# Revit family: ALW-L_приток
name_source: partatom
category: Воздухораспределители
revit_build: Autodesk Revit 2014 (Build: 20130308_1515(x64)
units: mm (PartAtom-declared; Revit-internal decimal feet)

## types (1242) — shared parameters
A = 23 мм
URL = http://inplast.ru
margins = 10 мм
Изготовитель = INPLAST-SMAY
Описание = Однорядная решетка с горизонтальными направляющими

## per-type parameters (varying)
| type | Aef | C' | D | n | С | Тип крепежа |
| ALW-L-100х100-АL | 0.006 м² | 95 мм | 100 мм | 10 | 100 мм | саморезы |
| ALW-L-125х100-АL | 0.008 м² | 120 мм | 100 мм | 10 | 125 мм | саморезы |
| ALW-L-125х125-АL | 0.009 м² | 120 мм | 125 мм | 13 | 125 мм | саморезы |
| ALW-L-150х100-АL | 0.009 м² | 145 мм | 100 мм | 10 | 150 мм | саморезы |
| ALW-L-150х125-АL | 0.011 м² | 145 мм | 125 мм | 13 | 150 мм | саморезы |
| ALW-L-150х150-АL | 0.014 м² | 145 мм | 150 мм | 15 | 150 мм | саморезы |
| ALW-L-200х100-АL | 0.012 м² | 195 мм | 100 мм | 10 | 200 мм | саморезы |
| ALW-L-200х125-АL | 0.015 м² | 195 мм | 125 мм | 13 | 200 мм | саморезы |
| ALW-L-200х150-АL | 0.018 м² | 195 мм | 150 мм | 15 | 200 мм | саморезы |
| ALW-L-200х200-АL | 0.024 м² | 195 мм | 200 мм | 20 | 200 мм | саморезы |
| ALW-L-225х100-АL | 0.014 м² | 220 мм | 100 мм | 10 | 225 мм | саморезы |
| ALW-L-225х125-АL | 0.017 м² | 220 мм | 125 мм | 13 | 225 мм | саморезы |
| ALW-L-225х150-АL | 0.020 м² | 220 мм | 150 мм | 15 | 225 мм | саморезы |
| ALW-L-225х200-АL | 0.027 м² | 220 мм | 200 мм | 20 | 225 мм | саморезы |
| ALW-L-225х225-АL | 0.030 м² | 220 мм | 225 мм | 23 | 225 мм | саморезы |
| ALW-L-250х100-АL | 0.015 м² | 245 мм | 100 мм | 10 | 250 мм | саморезы |
| ALW-L-250х125-АL | 0.019 м² | 245 мм | 125 мм | 13 | 250 мм | саморезы |
| ALW-L-250х150-АL | 0.023 м² | 245 мм | 150 мм | 15 | 250 мм | саморезы |
| ALW-L-250х200-АL | 0.030 м² | 245 мм | 200 мм | 20 | 250 мм | саморезы |
| ALW-L-250х225-АL | 0.034 м² | 245 мм | 225 мм | 23 | 250 мм | саморезы |
| ALW-L-250х250-АL | 0.038 м² | 245 мм | 250 мм | 25 | 250 мм | саморезы |
| ALW-L-300х100-АL | 0.018 м² | 295 мм | 100 мм | 10 | 300 мм | саморезы |
| ALW-L-300х125-АL | 0.023 м² | 295 мм | 125 мм | 13 | 300 мм | саморезы |
| ALW-L-300х150-АL | 0.027 м² | 295 мм | 150 мм | 15 | 300 мм | саморезы |
| ALW-L-300х200-АL | 0.036 м² | 295 мм | 200 мм | 20 | 300 мм | саморезы |
| ALW-L-300х225-АL | 0.041 м² | 295 мм | 225 мм | 23 | 300 мм | саморезы |
| ALW-L-300х250-АL | 0.045 м² | 295 мм | 250 мм | 25 | 300 мм | саморезы |
| ALW-L-300х300-АL | 0.054 м² | 295 мм | 300 мм | 30 | 300 мм | саморезы |
| ALW-L-325х100-АL | 0.020 м² | 320 мм | 100 мм | 10 | 325 мм | саморезы |
| ALW-L-325х125-АL | 0.024 м² | 320 мм | 125 мм | 13 | 325 мм | саморезы |
| ALW-L-325х150-АL | 0.029 м² | 320 мм | 150 мм | 15 | 325 мм | саморезы |
| ALW-L-325х200-АL | 0.039 м² | 320 мм | 200 мм | 20 | 325 мм | саморезы |
| ALW-L-325х225-АL | 0.044 м² | 320 мм | 225 мм | 23 | 325 мм | саморезы |
| ALW-L-325х250-АL | 0.049 м² | 320 мм | 250 мм | 25 | 325 мм | саморезы |
| ALW-L-325х300-АL | 0.059 м² | 320 мм | 300 мм | 30 | 325 мм | саморезы |
| ALW-L-325х325-АL | 0.064 м² | 320 мм | 325 мм | 33 | 325 мм | саморезы |
| ALW-L-350х100-АL | 0.021 м² | 345 мм | 100 мм | 10 | 350 мм | саморезы |
| ALW-L-350х125-АL | 0.026 м² | 345 мм | 125 мм | 13 | 350 мм | саморезы |
| ALW-L-350х150-АL | 0.032 м² | 345 мм | 150 мм | 15 | 350 мм | саморезы |
| ALW-L-350х200-АL | 0.042 м² | 345 мм | 200 мм | 20 | 350 мм | саморезы |
| ALW-L-350х225-АL | 0.047 м² | 345 мм | 225 мм | 23 | 350 мм | саморезы |
| ALW-L-350х250-АL | 0.053 м² | 345 мм | 250 мм | 25 | 350 мм | саморезы |
| ALW-L-350х300-АL | 0.063 м² | 345 мм | 300 мм | 30 | 350 мм | саморезы |
| ALW-L-350х325-АL | 0.068 м² | 345 мм | 325 мм | 33 | 350 мм | саморезы |
| ALW-L-350х350-АL | 0.074 м² | 345 мм | 350 мм | 35 | 350 мм | саморезы |
| ALW-L-400х100-АL | 0.024 м² | 395 мм | 100 мм | 10 | 400 мм | саморезы |
| ALW-L-400х125-АL | 0.030 м² | 395 мм | 125 мм | 13 | 400 мм | саморезы |
| ALW-L-400х150-АL | 0.036 м² | 395 мм | 150 мм | 15 | 400 мм | саморезы |
| ALW-L-400х200-АL | 0.048 м² | 395 мм | 200 мм | 20 | 400 мм | саморезы |
| ALW-L-400х225-АL | 0.054 м² | 395 мм | 225 мм | 23 | 400 мм | саморезы |
| ALW-L-400х250-АL | 0.060 м² | 395 мм | 250 мм | 25 | 400 мм | саморезы |
| ALW-L-400х300-АL | 0.072 м² | 395 мм | 300 мм | 30 | 400 мм | саморезы |
| ALW-L-400х325-АL | 0.078 м² | 395 мм | 325 мм | 33 | 400 мм | саморезы |
| ALW-L-400х350-АL | 0.084 м² | 395 мм | 350 мм | 35 | 400 мм | саморезы |
| ALW-L-400х400-АL | 0.096 м² | 395 мм | 400 мм | 40 | 400 мм | саморезы |
| ALW-L-425х100-АL | 0.026 м² | 420 мм | 100 мм | 10 | 425 мм | саморезы |
| ALW-L-425х125-АL | 0.032 м² | 420 мм | 125 мм | 13 | 425 мм | саморезы |
| ALW-L-425х150-АL | 0.038 м² | 420 мм | 150 мм | 15 | 425 мм | саморезы |
| ALW-L-425х200-АL | 0.051 м² | 420 мм | 200 мм | 20 | 425 мм | саморезы |
| ALW-L-425х225-АL | 0.058 м² | 420 мм | 225 мм | 23 | 425 мм | саморезы |
| ALW-L-425х250-АL | 0.064 м² | 420 мм | 250 мм | 25 | 425 мм | саморезы |
| ALW-L-425х300-АL | 0.077 м² | 420 мм | 300 мм | 30 | 425 мм | саморезы |
| ALW-L-425х325-АL | 0.083 м² | 420 мм | 325 мм | 33 | 425 мм | саморезы |
| ALW-L-425х350-АL | 0.089 м² | 420 мм | 350 мм | 35 | 425 мм | саморезы |
| ALW-L-425х400-АL | 0.102 м² | 420 мм | 400 мм | 40 | 425 мм | саморезы |
| ALW-L-425х425-АL | 0.109 м² | 420 мм | 425 мм | 43 | 425 мм | саморезы |
| ALW-L-450х100-АL | 0.027 м² | 445 мм | 100 мм | 10 | 450 мм | саморезы |
| ALW-L-450х125-АL | 0.034 м² | 445 мм | 125 мм | 13 | 450 мм | саморезы |
| ALW-L-450х150-АL | 0.041 м² | 445 мм | 150 мм | 15 | 450 мм | саморезы |
| ALW-L-450х200-АL | 0.054 м² | 445 мм | 200 мм | 20 | 450 мм | саморезы |
| ALW-L-450х225-АL | 0.061 м² | 445 мм | 225 мм | 23 | 450 мм | саморезы |
| ALW-L-450х250-АL | 0.068 м² | 445 мм | 250 мм | 25 | 450 мм | саморезы |
| ALW-L-450х300-АL | 0.081 м² | 445 мм | 300 мм | 30 | 450 мм | саморезы |
| ALW-L-450х325-АL | 0.088 м² | 445 мм | 325 мм | 33 | 450 мм | саморезы |
| ALW-L-450х350-АL | 0.095 м² | 445 мм | 350 мм | 35 | 450 мм | саморезы |
| ALW-L-450х400-АL | 0.108 м² | 445 мм | 400 мм | 40 | 450 мм | саморезы |
| ALW-L-450х425-АL | 0.115 м² | 445 мм | 425 мм | 43 | 450 мм | саморезы |
| ALW-L-450х450-АL | 0.122 м² | 445 мм | 450 мм | 45 | 450 мм | саморезы |
| ALW-L-500х100-АL | 0.030 м² | 495 мм | 100 мм | 10 | 500 мм | саморезы |
| ALW-L-500х125-АL | 0.038 м² | 495 мм | 125 мм | 13 | 500 мм | саморезы |
| ALW-L-500х150-АL | 0.045 м² | 495 мм | 150 мм | 15 | 500 мм | саморезы |
| ALW-L-500х200-АL | 0.060 м² | 495 мм | 200 мм | 20 | 500 мм | саморезы |
| ALW-L-500х225-АL | 0.068 м² | 495 мм | 225 мм | 23 | 500 мм | саморезы |
| ALW-L-500х250-АL | 0.075 м² | 495 мм | 250 мм | 25 | 500 мм | саморезы |
| ALW-L-500х300-АL | 0.090 м² | 495 мм | 300 мм | 30 | 500 мм | саморезы |
| ALW-L-500х325-АL | 0.098 м² | 495 мм | 325 мм | 33 | 500 мм | саморезы |
| ALW-L-500х350-АL | 0.105 м² | 495 мм | 350 мм | 35 | 500 мм | саморезы |
| ALW-L-500х400-АL | 0.120 м² | 495 мм | 400 мм | 40 | 500 мм | саморезы |
| ALW-L-500х425-АL | 0.128 м² | 495 мм | 425 мм | 43 | 500 мм | саморезы |
| ALW-L-500х450-АL | 0.135 м² | 495 мм | 450 мм | 45 | 500 мм | саморезы |
| ALW-L-500х500-АL | 0.150 м² | 495 мм | 500 мм | 50 | 500 мм | саморезы |
| ALW-L-525х100-АL | 0.032 м² | 520 мм | 100 мм | 10 | 525 мм | саморезы |
| ALW-L-525х125-АL | 0.039 м² | 520 мм | 125 мм | 13 | 525 мм | саморезы |
| ALW-L-525х150-АL | 0.047 м² | 520 мм | 150 мм | 15 | 525 мм | саморезы |
| ALW-L-525х200-АL | 0.063 м² | 520 мм | 200 мм | 20 | 525 мм | саморезы |
| ALW-L-525х225-АL | 0.071 м² | 520 мм | 225 мм | 23 | 525 мм | саморезы |
| ALW-L-525х250-АL | 0.079 м² | 520 мм | 250 мм | 25 | 525 мм | саморезы |
| ALW-L-525х300-АL | 0.095 м² | 520 мм | 300 мм | 30 | 525 мм | саморезы |
| ALW-L-525х325-АL | 0.103 м² | 520 мм | 325 мм | 33 | 525 мм | саморезы |
| ALW-L-525х350-АL | 0.111 м² | 520 мм | 350 мм | 35 | 525 мм | саморезы |
| ALW-L-525х400-АL | 0.126 м² | 520 мм | 400 мм | 40 | 525 мм | саморезы |
| ALW-L-525х425-АL | 0.134 м² | 520 мм | 425 мм | 43 | 525 мм | саморезы |
| ALW-L-525х450-АL | 0.142 м² | 520 мм | 450 мм | 45 | 525 мм | саморезы |
| ALW-L-525х500-АL | 0.158 м² | 520 мм | 500 мм | 50 | 525 мм | саморезы |
| ALW-L-525х525-АL | 0.166 м² | 520 мм | 525 мм | 53 | 525 мм | саморезы |
| ALW-L-550х100-АL | 0.033 м² | 545 мм | 100 мм | 10 | 550 мм | саморезы |
| ALW-L-550х125-АL | 0.041 м² | 545 мм | 125 мм | 13 | 550 мм | саморезы |
| ALW-L-550х150-АL | 0.050 м² | 545 мм | 150 мм | 15 | 550 мм | саморезы |
| ALW-L-550х200-АL | 0.066 м² | 545 мм | 200 мм | 20 | 550 мм | саморезы |
| ALW-L-550х225-АL | 0.074 м² | 545 мм | 225 мм | 23 | 550 мм | саморезы |
| ALW-L-550х250-АL | 0.083 м² | 545 мм | 250 мм | 25 | 550 мм | саморезы |
| ALW-L-550х300-АL | 0.099 м² | 545 мм | 300 мм | 30 | 550 мм | саморезы |
| ALW-L-550х325-АL | 0.108 м² | 545 мм | 325 мм | 33 | 550 мм | саморезы |
| ALW-L-550х350-АL | 0.116 м² | 545 мм | 350 мм | 35 | 550 мм | саморезы |
| ALW-L-550х400-АL | 0.132 м² | 545 мм | 400 мм | 40 | 550 мм | саморезы |
| ALW-L-550х425-АL | 0.141 м² | 545 мм | 425 мм | 43 | 550 мм | саморезы |
| ALW-L-550х450-АL | 0.149 м² | 545 мм | 450 мм | 45 | 550 мм | саморезы |
| ALW-L-550х500-АL | 0.165 м² | 545 мм | 500 мм | 50 | 550 мм | саморезы |
| ALW-L-550х525-АL | 0.174 м² | 545 мм | 525 мм | 53 | 550 мм | саморезы |
| ALW-L-550х550-АL | 0.182 м² | 545 мм | 550 мм | 55 | 550 мм | саморезы |
| ALW-L-600х100-АL | 0.036 м² | 595 мм | 100 мм | 10 | 600 мм | саморезы |
| ALW-L-600х125-АL | 0.045 м² | 595 мм | 125 мм | 13 | 600 мм | саморезы |
| ALW-L-600х150-АL | 0.054 м² | 595 мм | 150 мм | 15 | 600 мм | саморезы |
| ALW-L-600х200-АL | 0.072 м² | 595 мм | 200 мм | 20 | 600 мм | саморезы |
| ALW-L-600х225-АL | 0.081 м² | 595 мм | 225 мм | 23 | 600 мм | саморезы |
| ALW-L-600х250-АL | 0.090 м² | 595 мм | 250 мм | 25 | 600 мм | саморезы |
| ALW-L-600х300-АL | 0.108 м² | 595 мм | 300 мм | 30 | 600 мм | саморезы |
| ALW-L-600х325-АL | 0.117 м² | 595 мм | 325 мм | 33 | 600 мм | саморезы |
| ALW-L-600х350-АL | 0.126 м² | 595 мм | 350 мм | 35 | 600 мм | саморезы |
| ALW-L-600х400-АL | 0.144 м² | 595 мм | 400 мм | 40 | 600 мм | саморезы |
| ALW-L-600х425-АL | 0.153 м² | 595 мм | 425 мм | 43 | 600 мм | саморезы |
| ALW-L-600х450-АL | 0.162 м² | 595 мм | 450 мм | 45 | 600 мм | саморезы |
| ALW-L-600х500-АL | 0.180 м² | 595 мм | 500 мм | 50 | 600 мм | саморезы |
| ALW-L-600х525-АL | 0.190 м² | 595 мм | 525 мм | 53 | 600 мм | саморезы |
| ALW-L-600х550-АL | 0.199 м² | 595 мм | 550 мм | 55 | 600 мм | саморезы |
| ALW-L-600х600-АL | 0.217 м² | 595 мм | 600 мм | 60 | 600 мм | саморезы |
| ALW-L-625х100-АL | 0.038 м² | 620 мм | 100 мм | 10 | 625 мм | саморезы |
| ALW-L-625х125-АL | 0.047 м² | 620 мм | 125 мм | 13 | 625 мм | саморезы |
| ALW-L-625х150-АL | 0.056 м² | 620 мм | 150 мм | 15 | 625 мм | саморезы |
| ALW-L-625х200-АL | 0.075 м² | 620 мм | 200 мм | 20 | 625 мм | саморезы |
| ALW-L-625х225-АL | 0.085 м² | 620 мм | 225 мм | 23 | 625 мм | саморезы |
| ALW-L-625х250-АL | 0.094 м² | 620 мм | 250 мм | 25 | 625 мм | саморезы |
| ALW-L-625х300-АL | 0.113 м² | 620 мм | 300 мм | 30 | 625 мм | саморезы |
| ALW-L-625х325-АL | 0.122 м² | 620 мм | 325 мм | 33 | 625 мм | саморезы |
| ALW-L-625х350-АL | 0.132 м² | 620 мм | 350 мм | 35 | 625 мм | саморезы |
| ALW-L-625х400-АL | 0.150 м² | 620 мм | 400 мм | 40 | 625 мм | саморезы |
| ALW-L-625х425-АL | 0.160 м² | 620 мм | 425 мм | 43 | 625 мм | саморезы |
| ALW-L-625х450-АL | 0.169 м² | 620 мм | 450 мм | 45 | 625 мм | саморезы |
| ALW-L-625х500-АL | 0.188 м² | 620 мм | 500 мм | 50 | 625 мм | саморезы |
| ALW-L-625х525-АL | 0.197 м² | 620 мм | 525 мм | 53 | 625 мм | саморезы |
| ALW-L-625х550-АL | 0.207 м² | 620 мм | 550 мм | 55 | 625 мм | саморезы |
| ALW-L-625х600-АL | 0.226 м² | 620 мм | 600 мм | 60 | 625 мм | саморезы |
| ALW-L-625х625-АL | 0.235 м² | 620 мм | 625 мм | 63 | 625 мм | саморезы |
| ALW-L-650х100-АL | 0.039 м² | 645 мм | 100 мм | 10 | 650 мм | саморезы |
| ALW-L-650х125-АL | 0.049 м² | 645 мм | 125 мм | 13 | 650 мм | саморезы |
| ALW-L-650х150-АL | 0.059 м² | 645 мм | 150 мм | 15 | 650 мм | саморезы |
| ALW-L-650х200-АL | 0.078 м² | 645 мм | 200 мм | 20 | 650 мм | саморезы |
| ALW-L-650х225-АL | 0.088 м² | 645 мм | 225 мм | 23 | 650 мм | саморезы |
| ALW-L-650х250-АL | 0.098 м² | 645 мм | 250 мм | 25 | 650 мм | саморезы |
| ALW-L-650х300-АL | 0.117 м² | 645 мм | 300 мм | 30 | 650 мм | саморезы |
| ALW-L-650х325-АL | 0.127 м² | 645 мм | 325 мм | 33 | 650 мм | саморезы |
| ALW-L-650х350-АL | 0.137 м² | 645 мм | 350 мм | 35 | 650 мм | саморезы |
| ALW-L-650х400-АL | 0.156 м² | 645 мм | 400 мм | 40 | 650 мм | саморезы |
| ALW-L-650х425-АL | 0.166 м² | 645 мм | 425 мм | 43 | 650 мм | саморезы |
| ALW-L-650х450-АL | 0.176 м² | 645 мм | 450 мм | 45 | 650 мм | саморезы |
| ALW-L-650х500-АL | 0.196 м² | 645 мм | 500 мм | 50 | 650 мм | саморезы |
| ALW-L-650х525-АL | 0.205 м² | 645 мм | 525 мм | 53 | 650 мм | саморезы |
| ALW-L-650х550-АL | 0.215 м² | 645 мм | 550 мм | 55 | 650 мм | саморезы |
| ALW-L-650х600-АL | 0.235 м² | 645 мм | 600 мм | 60 | 650 мм | саморезы |
| ALW-L-650х625-АL | 0.244 м² | 645 мм | 625 мм | 63 | 650 мм | саморезы |
| ALW-L-650х650-АL | 0.254 м² | 645 мм | 650 мм | 65 | 650 мм | саморезы |
| ALW-L-700х100-АL | 0.042 м² | 695 мм | 100 мм | 10 | 700 мм | саморезы |
| ALW-L-700х125-АL | 0.053 м² | 695 мм | 125 мм | 13 | 700 мм | саморезы |
| ALW-L-700х150-АL | 0.063 м² | 695 мм | 150 мм | 15 | 700 мм | саморезы |
| ALW-L-700х200-АL | 0.084 м² | 695 мм | 200 мм | 20 | 700 мм | саморезы |
| ALW-L-700х225-АL | 0.095 м² | 695 мм | 225 мм | 23 | 700 мм | саморезы |
| ALW-L-700х250-АL | 0.105 м² | 695 мм | 250 мм | 25 | 700 мм | саморезы |
| ALW-L-700х300-АL | 0.126 м² | 695 мм | 300 мм | 30 | 700 мм | саморезы |
| ALW-L-700х325-АL | 0.137 м² | 695 мм | 325 мм | 33 | 700 мм | саморезы |
| ALW-L-700х350-АL | 0.147 м² | 695 мм | 350 мм | 35 | 700 мм | саморезы |
| ALW-L-700х400-АL | 0.168 м² | 695 мм | 400 мм | 40 | 700 мм | саморезы |
| ALW-L-700х425-АL | 0.179 м² | 695 мм | 425 мм | 43 | 700 мм | саморезы |
| ALW-L-700х450-АL | 0.190 м² | 695 мм | 450 мм | 45 | 700 мм | саморезы |
| ALW-L-700х500-АL | 0.211 м² | 695 мм | 500 мм | 50 | 700 мм | саморезы |
| ALW-L-700х525-АL | 0.221 м² | 695 мм | 525 мм | 53 | 700 мм | саморезы |
| ALW-L-700х550-АL | 0.232 м² | 695 мм | 550 мм | 55 | 700 мм | саморезы |
| ALW-L-700х600-АL | 0.253 м² | 695 мм | 600 мм | 60 | 700 мм | саморезы |
| ALW-L-700х625-АL | 0.263 м² | 695 мм | 625 мм | 63 | 700 мм | саморезы |
| ALW-L-700х650-АL | 0.274 м² | 695 мм | 650 мм | 65 | 700 мм | саморезы |
| ALW-L-725х100-АL | 0.044 м² | 720 мм | 100 мм | 10 | 725 мм | саморезы |
| ALW-L-725х125-АL | 0.055 м² | 720 мм | 125 мм | 13 | 725 мм | саморезы |
| ALW-L-725х150-АL | 0.065 м² | 720 мм | 150 мм | 15 | 725 мм | саморезы |
| ALW-L-725х200-АL | 0.087 м² | 720 мм | 200 мм | 20 | 725 мм | саморезы |
| ALW-L-725х225-АL | 0.098 м² | 720 мм | 225 мм | 23 | 725 мм | саморезы |
| ALW-L-725х250-АL | 0.109 м² | 720 мм | 250 мм | 25 | 725 мм | саморезы |
| ALW-L-725х300-АL | 0.131 м² | 720 мм | 300 мм | 30 | 725 мм | саморезы |
| ALW-L-725х325-АL | 0.142 м² | 720 мм | 325 мм | 33 | 725 мм | саморезы |
| ALW-L-725х350-АL | 0.153 м² | 720 мм | 350 мм | 35 | 725 мм | саморезы |
| ALW-L-725х400-АL | 0.174 м² | 720 мм | 400 мм | 40 | 725 мм | саморезы |
| ALW-L-725х425-АL | 0.185 м² | 720 мм | 425 мм | 43 | 725 мм | саморезы |
| ALW-L-725х450-АL | 0.196 м² | 720 мм | 450 мм | 45 | 725 мм | саморезы |
| ALW-L-725х500-АL | 0.218 м² | 720 мм | 500 мм | 50 | 725 мм | саморезы |
| ALW-L-725х525-АL | 0.229 м² | 720 мм | 525 мм | 53 | 725 мм | саморезы |
| ALW-L-725х550-АL | 0.240 м² | 720 мм | 550 мм | 55 | 725 мм | саморезы |
| ALW-L-725х600-АL | 0.262 м² | 720 мм | 600 мм | 60 | 725 мм | саморезы |
| ALW-L-725х625-АL | 0.273 м² | 720 мм | 625 мм | 63 | 725 мм | саморезы |
| ALW-L-725х650-АL | 0.284 м² | 720 мм | 650 мм | 65 | 725 мм | саморезы |
| ALW-L-750х100-АL | 0.045 м² | 745 мм | 100 мм | 10 | 750 мм | саморезы |
| ALW-L-750х125-АL | 0.056 м² | 745 мм | 125 мм | 13 | 750 мм | саморезы |
| ALW-L-750х150-АL | 0.068 м² | 745 мм | 150 мм | 15 | 750 мм | саморезы |
| ALW-L-750х200-АL | 0.090 м² | 745 мм | 200 мм | 20 | 750 мм | саморезы |
| ALW-L-750х225-АL | 0.102 м² | 745 мм | 225 мм | 23 | 750 мм | саморезы |
| ALW-L-750х250-АL | 0.113 м² | 745 мм | 250 мм | 25 | 750 мм | саморезы |
| ALW-L-750х300-АL | 0.135 м² | 745 мм | 300 мм | 30 | 750 мм | саморезы |
| ALW-L-750х325-АL | 0.147 м² | 745 мм | 325 мм | 33 | 750 мм | саморезы |
| ALW-L-750х350-АL | 0.158 м² | 745 мм | 350 мм | 35 | 750 мм | саморезы |
| ALW-L-750х400-АL | 0.180 м² | 745 мм | 400 мм | 40 | 750 мм | саморезы |
| ALW-L-750х425-АL | 0.192 м² | 745 мм | 425 мм | 43 | 750 мм | саморезы |
| ALW-L-750х450-АL | 0.203 м² | 745 мм | 450 мм | 45 | 750 мм | саморезы |
| ALW-L-750х500-АL | 0.226 м² | 745 мм | 500 мм | 50 | 750 мм | саморезы |
| ALW-L-750х525-АL | 0.237 м² | 745 мм | 525 мм | 53 | 750 мм | саморезы |
| ALW-L-750х550-АL | 0.248 м² | 745 мм | 550 мм | 55 | 750 мм | саморезы |
| ALW-L-750х600-АL | 0.271 м² | 745 мм | 600 мм | 60 | 750 мм | саморезы |
| ALW-L-750х625-АL | 0.282 м² | 745 мм | 625 мм | 63 | 750 мм | саморезы |
| ALW-L-750х650-АL | 0.293 м² | 745 мм | 650 мм | 65 | 750 мм | саморезы |
| ALW-L-800х100-АL | 0.048 м² | 795 мм | 100 мм | 10 | 800 мм | саморезы |
| ALW-L-800х125-АL | 0.060 м² | 795 мм | 125 мм | 13 | 800 мм | саморезы |
| ALW-L-800х150-АL | 0.072 м² | 795 мм | 150 мм | 15 | 800 мм | саморезы |
| ALW-L-800х200-АL | 0.096 м² | 795 мм | 200 мм | 20 | 800 мм | саморезы |
| ALW-L-800х225-АL | 0.108 м² | 795 мм | 225 мм | 23 | 800 мм | саморезы |
| ALW-L-800х250-АL | 0.120 м² | 795 мм | 250 мм | 25 | 800 мм | саморезы |
| ALW-L-800х300-АL | 0.144 м² | 795 мм | 300 мм | 30 | 800 мм | саморезы |
| ALW-L-800х325-АL | 0.156 м² | 795 мм | 325 мм | 33 | 800 мм | саморезы |
| ALW-L-800х350-АL | 0.168 м² | 795 мм | 350 мм | 35 | 800 мм | саморезы |
| ALW-L-800х400-АL | 0.193 м² | 795 мм | 400 мм | 40 | 800 мм | саморезы |
| ALW-L-800х425-АL | 0.205 м² | 795 мм | 425 мм | 43 | 800 мм | саморезы |
| ALW-L-800х450-АL | 0.217 м² | 795 мм | 450 мм | 45 | 800 мм | саморезы |
| ALW-L-800х500-АL | 0.241 м² | 795 мм | 500 мм | 50 | 800 мм | саморезы |
| ALW-L-800х525-АL | 0.253 м² | 795 мм | 525 мм | 53 | 800 мм | саморезы |
| ALW-L-800х550-АL | 0.265 м² | 795 мм | 550 мм | 55 | 800 мм | саморезы |
| ALW-L-800х600-АL | 0.289 м² | 795 мм | 600 мм | 60 | 800 мм | саморезы |
| ALW-L-800х625-АL | 0.301 м² | 795 мм | 625 мм | 63 | 800 мм | саморезы |
| ALW-L-800х650-АL | 0.313 м² | 795 мм | 650 мм | 65 | 800 мм | саморезы |
| ALW-L-825х100-АL | 0.050 м² | 820 мм | 100 мм | 10 | 825 мм | саморезы |
| ALW-L-825х125-АL | 0.062 м² | 820 мм | 125 мм | 13 | 825 мм | саморезы |
| ALW-L-825х150-АL | 0.074 м² | 820 мм | 150 мм | 15 | 825 мм | саморезы |
| ALW-L-825х200-АL | 0.099 м² | 820 мм | 200 мм | 20 | 825 мм | саморезы |
| ALW-L-825х225-АL | 0.112 м² | 820 мм | 225 мм | 23 | 825 мм | саморезы |
| ALW-L-825х250-АL | 0.124 м² | 820 мм | 250 мм | 25 | 825 мм | саморезы |
| ALW-L-825х300-АL | 0.149 м² | 820 мм | 300 мм | 30 | 825 мм | саморезы |
| ALW-L-825х325-АL | 0.161 м² | 820 мм | 325 мм | 33 | 825 мм | саморезы |
| ALW-L-825х350-АL | 0.174 м² | 820 мм | 350 мм | 35 | 825 мм | саморезы |
| ALW-L-825х400-АL | 0.199 м² | 820 мм | 400 мм | 40 | 825 мм | саморезы |
| ALW-L-825х425-АL | 0.211 м² | 820 мм | 425 мм | 43 | 825 мм | саморезы |
| ALW-L-825х450-АL | 0.223 м² | 820 мм | 450 мм | 45 | 825 мм | саморезы |
| ALW-L-825х500-АL | 0.248 м² | 820 мм | 500 мм | 50 | 825 мм | саморезы |
| ALW-L-825х525-АL | 0.261 м² | 820 мм | 525 мм | 53 | 825 мм | саморезы |
| ALW-L-825х550-АL | 0.273 м² | 820 мм | 550 мм | 55 | 825 мм | саморезы |
| ALW-L-825х600-АL | 0.298 м² | 820 мм | 600 мм | 60 | 825 мм | саморезы |
| ALW-L-825х625-АL | 0.310 м² | 820 мм | 625 мм | 63 | 825 мм | саморезы |
| ALW-L-825х650-АL | 0.323 м² | 820 мм | 650 мм | 65 | 825 мм | саморезы |
| ALW-L-850х100-АL | 0.051 м² | 845 мм | 100 мм | 10 | 850 мм | саморезы |
| ALW-L-850х125-АL | 0.064 м² | 845 мм | 125 мм | 13 | 850 мм | саморезы |
| ALW-L-850х150-АL | 0.077 м² | 845 мм | 150 мм | 15 | 850 мм | саморезы |
| ALW-L-850х200-АL | 0.102 м² | 845 мм | 200 мм | 20 | 850 мм | саморезы |
| ALW-L-850х225-АL | 0.115 м² | 845 мм | 225 мм | 23 | 850 мм | саморезы |
| ALW-L-850х250-АL | 0.128 м² | 845 мм | 250 мм | 25 | 850 мм | саморезы |
| ALW-L-850х300-АL | 0.153 м² | 845 мм | 300 мм | 30 | 850 мм | саморезы |
| ALW-L-850х325-АL | 0.166 м² | 845 мм | 325 мм | 33 | 850 мм | саморезы |
| ALW-L-850х350-АL | 0.179 м² | 845 мм | 350 мм | 35 | 850 мм | саморезы |
| ALW-L-850х400-АL | 0.205 м² | 845 мм | 400 мм | 40 | 850 мм | саморезы |
| ALW-L-850х425-АL | 0.217 м² | 845 мм | 425 мм | 43 | 850 мм | саморезы |
| ALW-L-850х450-АL | 0.230 м² | 845 мм | 450 мм | 45 | 850 мм | саморезы |
| ALW-L-850х500-АL | 0.256 м² | 845 мм | 500 мм | 50 | 850 мм | саморезы |
| ALW-L-850х525-АL | 0.268 м² | 845 мм | 525 мм | 53 | 850 мм | саморезы |
| ALW-L-850х550-АL | 0.281 м² | 845 мм | 550 мм | 55 | 850 мм | саморезы |
| ALW-L-850х600-АL | 0.307 м² | 845 мм | 600 мм | 60 | 850 мм | саморезы |
| ALW-L-850х625-АL | 0.320 м² | 845 мм | 625 мм | 63 | 850 мм | саморезы |
| ALW-L-850х650-АL | 0.332 м² | 845 мм | 650 мм | 65 | 850 мм | саморезы |
| ALW-L-900х100-АL | 0.054 м² | 895 мм | 100 мм | 10 | 900 мм | саморезы |
| ALW-L-900х125-АL | 0.068 м² | 895 мм | 125 мм | 13 | 900 мм | саморезы |
| ALW-L-900х150-АL | 0.081 м² | 895 мм | 150 мм | 15 | 900 мм | саморезы |
| ALW-L-900х200-АL | 0.108 м² | 895 мм | 200 мм | 20 | 900 мм | саморезы |
| ALW-L-900х225-АL | 0.122 м² | 895 мм | 225 мм | 23 | 900 мм | саморезы |
| ALW-L-900х250-АL | 0.135 м² | 895 мм | 250 мм | 25 | 900 мм | саморезы |
| ALW-L-900х300-АL | 0.162 м² | 895 мм | 300 мм | 30 | 900 мм | саморезы |
| ALW-L-900х325-АL | 0.176 м² | 895 мм | 325 мм | 33 | 900 мм | саморезы |
| ALW-L-900х350-АL | 0.190 м² | 895 мм | 350 мм | 35 | 900 мм | саморезы |
| ALW-L-900х400-АL | 0.217 м² | 895 мм | 400 мм | 40 | 900 мм | саморезы |
| ALW-L-900х425-АL | 0.230 м² | 895 мм | 425 мм | 43 | 900 мм | саморезы |
| ALW-L-900х450-АL | 0.244 м² | 895 мм | 450 мм | 45 | 900 мм | саморезы |
| ALW-L-900х500-АL | 0.271 м² | 895 мм | 500 мм | 50 | 900 мм | саморезы |
| ALW-L-900х525-АL | 0.284 м² | 895 мм | 525 мм | 53 | 900 мм | саморезы |
| ALW-L-900х550-АL | 0.298 м² | 895 мм | 550 мм | 55 | 900 мм | саморезы |
| ALW-L-900х600-АL | 0.325 м² | 895 мм | 600 мм | 60 | 900 мм | саморезы |
| ALW-L-900х625-АL | 0.338 м² | 895 мм | 625 мм | 63 | 900 мм | саморезы |
| ALW-L-900х650-АL | 0.352 м² | 895 мм | 650 мм | 65 | 900 мм | саморезы |
| ALW-L-925х100-АL | 0.056 м² | 920 мм | 100 мм | 10 | 925 мм | саморезы |
| ALW-L-925х125-АL | 0.070 м² | 920 мм | 125 мм | 13 | 925 мм | саморезы |
| ALW-L-925х150-АL | 0.083 м² | 920 мм | 150 мм | 15 | 925 мм | саморезы |
| ALW-L-925х200-АL | 0.111 м² | 920 мм | 200 мм | 20 | 925 мм | саморезы |
| ALW-L-925х225-АL | 0.125 м² | 920 мм | 225 мм | 23 | 925 мм | саморезы |
| ALW-L-925х250-АL | 0.139 м² | 920 мм | 250 мм | 25 | 925 мм | саморезы |
| ALW-L-925х300-АL | 0.167 м² | 920 мм | 300 мм | 30 | 925 мм | саморезы |
| ALW-L-925х325-АL | 0.181 м² | 920 мм | 325 мм | 33 | 925 мм | саморезы |
| ALW-L-925х350-АL | 0.195 м² | 920 мм | 350 мм | 35 | 925 мм | саморезы |
| ALW-L-925х400-АL | 0.223 м² | 920 мм | 400 мм | 40 | 925 мм | саморезы |
| ALW-L-925х425-АL | 0.237 м² | 920 мм | 425 мм | 43 | 925 мм | саморезы |
| ALW-L-925х450-АL | 0.250 м² | 920 мм | 450 мм | 45 | 925 мм | саморезы |
| ALW-L-925х500-АL | 0.278 м² | 920 мм | 500 мм | 50 | 925 мм | саморезы |
| ALW-L-925х525-АL | 0.292 м² | 920 мм | 525 мм | 53 | 925 мм | саморезы |
| ALW-L-925х550-АL | 0.306 м² | 920 мм | 550 мм | 55 | 925 мм | саморезы |
| ALW-L-925х600-АL | 0.334 м² | 920 мм | 600 мм | 60 | 925 мм | саморезы |
| ALW-L-925х625-АL | 0.348 м² | 920 мм | 625 мм | 63 | 925 мм | саморезы |
| ALW-L-925х650-АL | 0.362 м² | 920 мм | 650 мм | 65 | 925 мм | саморезы |
| ALW-L-950х100-АL | 0.057 м² | 945 мм | 100 мм | 10 | 950 мм | саморезы |
| ALW-L-950х125-АL | 0.071 м² | 945 мм | 125 мм | 13 | 950 мм | саморезы |
| ALW-L-950х150-АL | 0.086 м² | 945 мм | 150 мм | 15 | 950 мм | саморезы |
| ALW-L-950х200-АL | 0.114 м² | 945 мм | 200 мм | 20 | 950 мм | саморезы |
| ALW-L-950х225-АL | 0.129 м² | 945 мм | 225 мм | 23 | 950 мм | саморезы |
| ALW-L-950х250-АL | 0.143 м² | 945 мм | 250 мм | 25 | 950 мм | саморезы |
| ALW-L-950х300-АL | 0.171 м² | 945 мм | 300 мм | 30 | 950 мм | саморезы |
| ALW-L-950х325-АL | 0.186 м² | 945 мм | 325 мм | 33 | 950 мм | саморезы |
| ALW-L-950х350-АL | 0.200 м² | 945 мм | 350 мм | 35 | 950 мм | саморезы |
| ALW-L-950х400-АL | 0.229 м² | 945 мм | 400 мм | 40 | 950 мм | саморезы |
| ALW-L-950х425-АL | 0.243 м² | 945 мм | 425 мм | 43 | 950 мм | саморезы |
| ALW-L-950х450-АL | 0.257 м² | 945 мм | 450 мм | 45 | 950 мм | саморезы |
| ALW-L-950х500-АL | 0.286 м² | 945 мм | 500 мм | 50 | 950 мм | саморезы |
| ALW-L-950х525-АL | 0.300 м² | 945 мм | 525 мм | 53 | 950 мм | саморезы |
| ALW-L-950х550-АL | 0.314 м² | 945 мм | 550 мм | 55 | 950 мм | саморезы |
| ALW-L-950х600-АL | 0.343 м² | 945 мм | 600 мм | 60 | 950 мм | саморезы |
| ALW-L-950х625-АL | 0.357 м² | 945 мм | 625 мм | 63 | 950 мм | саморезы |
| ALW-L-950х650-АL | 0.371 м² | 945 мм | 650 мм | 65 | 950 мм | саморезы |
| ALW-L-1000х100-АL | 0.060 м² | 995 мм | 100 мм | 10 | 1000 мм | саморезы |
| ALW-L-1000х125-АL | 0.075 м² | 995 мм | 125 мм | 13 | 1000 мм | саморезы |
| ALW-L-1000х150-АL | 0.090 м² | 995 мм | 150 мм | 15 | 1000 мм | саморезы |
| ALW-L-1000х200-АL | 0.120 м² | 995 мм | 200 мм | 20 | 1000 мм | саморезы |
| ALW-L-1000х225-АL | 0.135 м² | 995 мм | 225 мм | 23 | 1000 мм | саморезы |
| ALW-L-1000х250-АL | 0.150 м² | 995 мм | 250 мм | 25 | 1000 мм | саморезы |
| ALW-L-1000х300-АL | 0.180 м² | 995 мм | 300 мм | 30 | 1000 мм | саморезы |
| ALW-L-1000х325-АL | 0.196 м² | 995 мм | 325 мм | 33 | 1000 мм | саморезы |
| ALW-L-1000х350-АL | 0.211 м² | 995 мм | 350 мм | 35 | 1000 мм | саморезы |
| ALW-L-1000х400-АL | 0.241 м² | 995 мм | 400 мм | 40 | 1000 мм | саморезы |
| ALW-L-1000х425-АL | 0.256 м² | 995 мм | 425 мм | 43 | 1000 мм | саморезы |
| ALW-L-1000х450-АL | 0.271 м² | 995 мм | 450 мм | 45 | 1000 мм | саморезы |
| ALW-L-1000х500-АL | 0.301 м² | 995 мм | 500 мм | 50 | 1000 мм | саморезы |
| ALW-L-1000х525-АL | 0.316 м² | 995 мм | 525 мм | 53 | 1000 мм | саморезы |
| ALW-L-1000х550-АL | 0.331 м² | 995 мм | 550 мм | 55 | 1000 мм | саморезы |
| ALW-L-1000х600-АL | 0.361 м² | 995 мм | 600 мм | 60 | 1000 мм | саморезы |
| ALW-L-1000х625-АL | 0.376 м² | 995 мм | 625 мм | 63 | 1000 мм | саморезы |
| ALW-L-1000х650-АL | 0.391 м² | 995 мм | 650 мм | 65 | 1000 мм | саморезы |
| ALW-L-1025х100-АL | 0.062 м² | 1020 мм | 100 мм | 10 | 1025 мм | саморезы |
| ALW-L-1025х125-АL | 0.077 м² | 1020 мм | 125 мм | 13 | 1025 мм | саморезы |
| ALW-L-1025х150-АL | 0.092 м² | 1020 мм | 150 мм | 15 | 1025 мм | саморезы |
| ALW-L-1025х200-АL | 0.123 м² | 1020 мм | 200 мм | 20 | 1025 мм | саморезы |
| ALW-L-1025х225-АL | 0.139 м² | 1020 мм | 225 мм | 23 | 1025 мм | саморезы |
| ALW-L-1025х250-АL | 0.154 м² | 1020 мм | 250 мм | 25 | 1025 мм | саморезы |
| ALW-L-1025х300-АL | 0.185 м² | 1020 мм | 300 мм | 30 | 1025 мм | саморезы |
| ALW-L-1025х325-АL | 0.200 м² | 1020 мм | 325 мм | 33 | 1025 мм | саморезы |
| ALW-L-1025х350-АL | 0.216 м² | 1020 мм | 350 мм | 35 | 1025 мм | саморезы |
| ALW-L-1025х400-АL | 0.247 м² | 1020 мм | 400 мм | 40 | 1025 мм | саморезы |
| ALW-L-1025х425-АL | 0.262 м² | 1020 мм | 425 мм | 43 | 1025 мм | саморезы |
| ALW-L-1025х450-АL | 0.277 м² | 1020 мм | 450 мм | 45 | 1025 мм | саморезы |
| ALW-L-1025х500-АL | 0.308 м² | 1020 мм | 500 мм | 50 | 1025 мм | саморезы |
| ALW-L-1025х525-АL | 0.324 м² | 1020 мм | 525 мм | 53 | 1025 мм | саморезы |
| ALW-L-1025х550-АL | 0.339 м² | 1020 мм | 550 мм | 55 | 1025 мм | саморезы |
| ALW-L-1025х600-АL | 0.370 м² | 1020 мм | 600 мм | 60 | 1025 мм | саморезы |
| ALW-L-1025х625-АL | 0.385 м² | 1020 мм | 625 мм | 63 | 1025 мм | саморезы |
| ALW-L-1025х650-АL | 0.401 м² | 1020 мм | 650 мм | 65 | 1025 мм | саморезы |
| ALW-L-1050х100-АL | 0.063 м² | 1045 мм | 100 мм | 10 | 1050 мм | саморезы |
| ALW-L-1050х125-АL | 0.079 м² | 1045 мм | 125 мм | 13 | 1050 мм | саморезы |
| ALW-L-1050х150-АL | 0.095 м² | 1045 мм | 150 мм | 15 | 1050 мм | саморезы |
| ALW-L-1050х200-АL | 0.126 м² | 1045 мм | 200 мм | 20 | 1050 мм | саморезы |
| ALW-L-1050х225-АL | 0.142 м² | 1045 мм | 225 мм | 23 | 1050 мм | саморезы |
| ALW-L-1050х250-АL | 0.158 м² | 1045 мм | 250 мм | 25 | 1050 мм | саморезы |
| ALW-L-1050х300-АL | 0.190 м² | 1045 мм | 300 мм | 30 | 1050 мм | саморезы |
| ALW-L-1050х325-АL | 0.205 м² | 1045 мм | 325 мм | 33 | 1050 мм | саморезы |
| ALW-L-1050х350-АL | 0.221 м² | 1045 мм | 350 мм | 35 | 1050 мм | саморезы |
| ALW-L-1050х400-АL | 0.253 м² | 1045 мм | 400 мм | 40 | 1050 мм | саморезы |
| ALW-L-1050х425-АL | 0.268 м² | 1045 мм | 425 мм | 43 | 1050 мм | саморезы |
| ALW-L-1050х450-АL | 0.284 м² | 1045 мм | 450 мм | 45 | 1050 мм | саморезы |
| ALW-L-1050х500-АL | 0.316 м² | 1045 мм | 500 мм | 50 | 1050 мм | саморезы |
| ALW-L-1050х525-АL | 0.332 м² | 1045 мм | 525 мм | 53 | 1050 мм | саморезы |
| ALW-L-1050х550-АL | 0.347 м² | 1045 мм | 550 мм | 55 | 1050 мм | саморезы |
| ALW-L-1050х600-АL | 0.379 м² | 1045 мм | 600 мм | 60 | 1050 мм | саморезы |
| ALW-L-1050х625-АL | 0.395 м² | 1045 мм | 625 мм | 63 | 1050 мм | саморезы |
| ALW-L-1050х650-АL | 0.411 м² | 1045 мм | 650 мм | 65 | 1050 мм | саморезы |
| ALW-L-1100х100-АL | 0.066 м² | 1095 мм | 100 мм | 10 | 1100 мм | саморезы |
| ALW-L-1100х125-АL | 0.083 м² | 1095 мм | 125 мм | 13 | 1100 мм | саморезы |
| ALW-L-1100х150-АL | 0.099 м² | 1095 мм | 150 мм | 15 | 1100 мм | саморезы |
| ALW-L-1100х200-АL | 0.132 м² | 1095 мм | 200 мм | 20 | 1100 мм | саморезы |
| ALW-L-1100х225-АL | 0.149 м² | 1095 мм | 225 мм | 23 | 1100 мм | саморезы |
| ALW-L-1100х250-АL | 0.165 м² | 1095 мм | 250 мм | 25 | 1100 мм | саморезы |
| ALW-L-1100х300-АL | 0.199 м² | 1095 мм | 300 мм | 30 | 1100 мм | саморезы |
| ALW-L-1100х325-АL | 0.215 м² | 1095 мм | 325 мм | 33 | 1100 мм | саморезы |
| ALW-L-1100х350-АL | 0.232 м² | 1095 мм | 350 мм | 35 | 1100 мм | саморезы |
| ALW-L-1100х400-АL | 0.265 м² | 1095 мм | 400 мм | 40 | 1100 мм | саморезы |
| ALW-L-1100х425-АL | 0.281 м² | 1095 мм | 425 мм | 43 | 1100 мм | саморезы |
| ALW-L-1100х450-АL | 0.298 м² | 1095 мм | 450 мм | 45 | 1100 мм | саморезы |
| ALW-L-1100х500-АL | 0.331 м² | 1095 мм | 500 мм | 50 | 1100 мм | саморезы |
| ALW-L-1100х525-АL | 0.347 м² | 1095 мм | 525 мм | 53 | 1100 мм | саморезы |
| ALW-L-1100х550-АL | 0.364 м² | 1095 мм | 550 мм | 55 | 1100 мм | саморезы |
| ALW-L-1100х600-АL | 0.397 м² | 1095 мм | 600 мм | 60 | 1100 мм | саморезы |
| ALW-L-1100х625-АL | 0.414 м² | 1095 мм | 625 мм | 63 | 1100 мм | саморезы |
| ALW-L-1100х650-АL | 0.430 м² | 1095 мм | 650 мм | 65 | 1100 мм | саморезы |
| ALW-L-1125х100-АL | 0.068 м² | 1120 мм | 100 мм | 10 | 1125 мм | саморезы |
| ALW-L-1125х125-АL | 0.085 м² | 1120 мм | 125 мм | 13 | 1125 мм | саморезы |
| ALW-L-1125х150-АL | 0.102 м² | 1120 мм | 150 мм | 15 | 1125 мм | саморезы |
| ALW-L-1125х200-АL | 0.135 м² | 1120 мм | 200 мм | 20 | 1125 мм | саморезы |
| ALW-L-1125х225-АL | 0.152 м² | 1120 мм | 225 мм | 23 | 1125 мм | саморезы |
| ALW-L-1125х250-АL | 0.169 м² | 1120 мм | 250 мм | 25 | 1125 мм | саморезы |
| ALW-L-1125х300-АL | 0.203 м² | 1120 мм | 300 мм | 30 | 1125 мм | саморезы |
| ALW-L-1125х325-АL | 0.220 м² | 1120 мм | 325 мм | 33 | 1125 мм | саморезы |
| ALW-L-1125х350-АL | 0.237 м² | 1120 мм | 350 мм | 35 | 1125 мм | саморезы |
| ALW-L-1125х400-АL | 0.271 м² | 1120 мм | 400 мм | 40 | 1125 мм | саморезы |
| ALW-L-1125х425-АL | 0.288 м² | 1120 мм | 425 мм | 43 | 1125 мм | саморезы |
| ALW-L-1125х450-АL | 0.305 м² | 1120 мм | 450 мм | 45 | 1125 мм | саморезы |
| ALW-L-1125х500-АL | 0.338 м² | 1120 мм | 500 мм | 50 | 1125 мм | саморезы |
| ALW-L-1125х525-АL | 0.355 м² | 1120 мм | 525 мм | 53 | 1125 мм | саморезы |
| ALW-L-1125х550-АL | 0.372 м² | 1120 мм | 550 мм | 55 | 1125 мм | саморезы |
| ALW-L-1125х600-АL | 0.406 м² | 1120 мм | 600 мм | 60 | 1125 мм | саморезы |
| ALW-L-1125х625-АL | 0.423 м² | 1120 мм | 625 мм | 63 | 1125 мм | саморезы |
| ALW-L-1125х650-АL | 0.440 м² | 1120 мм | 650 мм | 65 | 1125 мм | саморезы |
| ALW-L-1150х100-АL | 0.069 м² | 1145 мм | 100 мм | 10 | 1150 мм | саморезы |
| ALW-L-1150х125-АL | 0.086 м² | 1145 мм | 125 мм | 13 | 1150 мм | саморезы |
| ALW-L-1150х150-АL | 0.104 м² | 1145 мм | 150 мм | 15 | 1150 мм | саморезы |
| ALW-L-1150х200-АL | 0.138 м² | 1145 мм | 200 мм | 20 | 1150 мм | саморезы |
| ALW-L-1150х225-АL | 0.156 м² | 1145 мм | 225 мм | 23 | 1150 мм | саморезы |
| ALW-L-1150х250-АL | 0.173 м² | 1145 мм | 250 мм | 25 | 1150 мм | саморезы |
| ALW-L-1150х300-АL | 0.208 м² | 1145 мм | 300 мм | 30 | 1150 мм | саморезы |
| ALW-L-1150х325-АL | 0.225 м² | 1145 мм | 325 мм | 33 | 1150 мм | саморезы |
| ALW-L-1150х350-АL | 0.242 м² | 1145 мм | 350 мм | 35 | 1150 мм | саморезы |
| ALW-L-1150х400-АL | 0.277 м² | 1145 мм | 400 мм | 40 | 1150 мм | саморезы |
| ALW-L-1150х425-АL | 0.294 м² | 1145 мм | 425 мм | 43 | 1150 мм | саморезы |
| ALW-L-1150х450-АL | 0.311 м² | 1145 мм | 450 мм | 45 | 1150 мм | саморезы |
| ALW-L-1150х500-АL | 0.346 м² | 1145 мм | 500 мм | 50 | 1150 мм | саморезы |
| ALW-L-1150х525-АL | 0.363 м² | 1145 мм | 525 мм | 53 | 1150 мм | саморезы |
| ALW-L-1150х550-АL | 0.381 м² | 1145 мм | 550 мм | 55 | 1150 мм | саморезы |
| ALW-L-1150х600-АL | 0.415 м² | 1145 мм | 600 мм | 60 | 1150 мм | саморезы |
| ALW-L-1150х625-АL | 0.432 м² | 1145 мм | 625 мм | 63 | 1150 мм | саморезы |
| ALW-L-1150х650-АL | 0.450 м² | 1145 мм | 650 мм | 65 | 1150 мм | саморезы |
| ALW-L-1200х100-АL | 0.072 м² | 1195 мм | 100 мм | 10 | 1200 мм | саморезы |
| ALW-L-1200х125-АL | 0.090 м² | 1195 мм | 125 мм | 13 | 1200 мм | саморезы |
| ALW-L-1200х150-АL | 0.108 м² | 1195 мм | 150 мм | 15 | 1200 мм | саморезы |
| ALW-L-1200х200-АL | 0.144 м² | 1195 мм | 200 мм | 20 | 1200 мм | саморезы |
| ALW-L-1200х225-АL | 0.162 м² | 1195 мм | 225 мм | 23 | 1200 мм | саморезы |
| ALW-L-1200х250-АL | 0.180 м² | 1195 мм | 250 мм | 25 | 1200 мм | саморезы |
| ALW-L-1200х300-АL | 0.217 м² | 1195 мм | 300 мм | 30 | 1200 мм | саморезы |
| ALW-L-1200х325-АL | 0.235 м² | 1195 мм | 325 мм | 33 | 1200 мм | саморезы |
| ALW-L-1200х350-АL | 0.253 м² | 1195 мм | 350 мм | 35 | 1200 мм | саморезы |
| ALW-L-1200х400-АL | 0.289 м² | 1195 мм | 400 мм | 40 | 1200 мм | саморезы |
| ALW-L-1200х425-АL | 0.307 м² | 1195 мм | 425 мм | 43 | 1200 мм | саморезы |
| ALW-L-1200х450-АL | 0.325 м² | 1195 мм | 450 мм | 45 | 1200 мм | саморезы |
| ALW-L-1200х500-АL | 0.361 м² | 1195 мм | 500 мм | 50 | 1200 мм | саморезы |
| ALW-L-1200х525-АL | 0.379 м² | 1195 мм | 525 мм | 53 | 1200 мм | саморезы |
| ALW-L-1200х550-АL | 0.397 м² | 1195 мм | 550 мм | 55 | 1200 мм | саморезы |
| ALW-L-1200х600-АL | 0.433 м² | 1195 мм | 600 мм | 60 | 1200 мм | саморезы |
| ALW-L-1200х625-АL | 0.451 м² | 1195 мм | 625 мм | 63 | 1200 мм | саморезы |
| ALW-L-1200х650-АL | 0.469 м² | 1195 мм | 650 мм | 65 | 1200 мм | саморезы |
| ALW-L-1225х100-АL | 0.074 м² | 1220 мм | 100 мм | 10 | 1225 мм | саморезы |
| ALW-L-1225х125-АL | 0.092 м² | 1220 мм | 125 мм | 13 | 1225 мм | саморезы |
| ALW-L-1225х150-АL | 0.111 м² | 1220 мм | 150 мм | 15 | 1225 мм | саморезы |
| ALW-L-1225х200-АL | 0.147 м² | 1220 мм | 200 мм | 20 | 1225 мм | саморезы |
| ALW-L-1225х225-АL | 0.166 м² | 1220 мм | 225 мм | 23 | 1225 мм | саморезы |
| ALW-L-1225х250-АL | 0.184 м² | 1220 мм | 250 мм | 25 | 1225 мм | саморезы |
| ALW-L-1225х300-АL | 0.221 м² | 1220 мм | 300 мм | 30 | 1225 мм | саморезы |
| ALW-L-1225х325-АL | 0.240 м² | 1220 мм | 325 мм | 33 | 1225 мм | саморезы |
| ALW-L-1225х350-АL | 0.258 м² | 1220 мм | 350 мм | 35 | 1225 мм | саморезы |
| ALW-L-1225х400-АL | 0.295 м² | 1220 мм | 400 мм | 40 | 1225 мм | саморезы |
| ALW-L-1225х425-АL | 0.313 м² | 1220 мм | 425 мм | 43 | 1225 мм | саморезы |
| ALW-L-1225х450-АL | 0.332 м² | 1220 мм | 450 мм | 45 | 1225 мм | саморезы |
| ALW-L-1225х500-АL | 0.368 м² | 1220 мм | 500 мм | 50 | 1225 мм | саморезы |
| ALW-L-1225х525-АL | 0.387 м² | 1220 мм | 525 мм | 53 | 1225 мм | саморезы |
| ALW-L-1225х550-АL | 0.405 м² | 1220 мм | 550 мм | 55 | 1225 мм | саморезы |
| ALW-L-1225х600-АL | 0.442 м² | 1220 мм | 600 мм | 60 | 1225 мм | саморезы |
| ALW-L-1225х625-АL | 0.461 м² | 1220 мм | 625 мм | 63 | 1225 мм | саморезы |
| ALW-L-1225х650-АL | 0.479 м² | 1220 мм | 650 мм | 65 | 1225 мм | саморезы |
| ALW-L-1250х100-АL | 0.075 м² | 1245 мм | 100 мм | 10 | 1250 мм | саморезы |
| ALW-L-1250х125-АL | 0.094 м² | 1245 мм | 125 мм | 13 | 1250 мм | саморезы |
| ALW-L-1250х150-АL | 0.113 м² | 1245 мм | 150 мм | 15 | 1250 мм | саморезы |
| ALW-L-1250х200-АL | 0.150 м² | 1245 мм | 200 мм | 20 | 1250 мм | саморезы |
| ALW-L-1250х225-АL | 0.169 м² | 1245 мм | 225 мм | 23 | 1250 мм | саморезы |
| ALW-L-1250х250-АL | 0.188 м² | 1245 мм | 250 мм | 25 | 1250 мм | саморезы |
| ALW-L-1250х300-АL | 0.226 м² | 1245 мм | 300 мм | 30 | 1250 мм | саморезы |
| ALW-L-1250х325-АL | 0.244 м² | 1245 мм | 325 мм | 33 | 1250 мм | саморезы |
| ALW-L-1250х350-АL | 0.263 м² | 1245 мм | 350 мм | 35 | 1250 мм | саморезы |
| ALW-L-1250х400-АL | 0.301 м² | 1245 мм | 400 мм | 40 | 1250 мм | саморезы |
| ALW-L-1250х425-АL | 0.320 м² | 1245 мм | 425 мм | 43 | 1250 мм | саморезы |
| ALW-L-1250х450-АL | 0.338 м² | 1245 мм | 450 мм | 45 | 1250 мм | саморезы |
| ALW-L-1250х500-АL | 0.376 м² | 1245 мм | 500 мм | 50 | 1250 мм | саморезы |
| ALW-L-1250х525-АL | 0.395 м² | 1245 мм | 525 мм | 53 | 1250 мм | саморезы |
| ALW-L-1250х550-АL | 0.414 м² | 1245 мм | 550 мм | 55 | 1250 мм | саморезы |
| ALW-L-1250х600-АL | 0.451 м² | 1245 мм | 600 мм | 60 | 1250 мм | саморезы |
| ALW-L-1250х625-АL | 0.470 м² | 1245 мм | 625 мм | 63 | 1250 мм | саморезы |
| ALW-L-1250х650-АL | 0.489 м² | 1245 мм | 650 мм | 65 | 1250 мм | саморезы |
| ALW-L-1300х100-АL | 0.078 м² | 1295 мм | 100 мм | 10 | 1300 мм | саморезы |
| ALW-L-1300х125-АL | 0.098 м² | 1295 мм | 125 мм | 13 | 1300 мм | саморезы |
| ALW-L-1300х150-АL | 0.117 м² | 1295 мм | 150 мм | 15 | 1300 мм | саморезы |
| ALW-L-1300х200-АL | 0.156 м² | 1295 мм | 200 мм | 20 | 1300 мм | саморезы |
| ALW-L-1300х225-АL | 0.176 м² | 1295 мм | 225 мм | 23 | 1300 мм | саморезы |
| ALW-L-1300х250-АL | 0.196 м² | 1295 мм | 250 мм | 25 | 1300 мм | саморезы |
| ALW-L-1300х300-АL | 0.235 м² | 1295 мм | 300 мм | 30 | 1300 мм | саморезы |
| ALW-L-1300х325-АL | 0.254 м² | 1295 мм | 325 мм | 33 | 1300 мм | саморезы |
| ALW-L-1300х350-АL | 0.274 м² | 1295 мм | 350 мм | 35 | 1300 мм | саморезы |
| ALW-L-1300х400-АL | 0.313 м² | 1295 мм | 400 мм | 40 | 1300 мм | саморезы |
| ALW-L-1300х425-АL | 0.332 м² | 1295 мм | 425 мм | 43 | 1300 мм | саморезы |
| ALW-L-1300х450-АL | 0.352 м² | 1295 мм | 450 мм | 45 | 1300 мм | саморезы |
| ALW-L-1300х500-АL | 0.391 м² | 1295 мм | 500 мм | 50 | 1300 мм | саморезы |
| ALW-L-1300х525-АL | 0.411 м² | 1295 мм | 525 мм | 53 | 1300 мм | саморезы |
| ALW-L-1300х550-АL | 0.430 м² | 1295 мм | 550 мм | 55 | 1300 мм | саморезы |
| ALW-L-1300х600-АL | 0.469 м² | 1295 мм | 600 мм | 60 | 1300 мм | саморезы |
| ALW-L-1300х625-АL | 0.489 м² | 1295 мм | 625 мм | 63 | 1300 мм | саморезы |
| ALW-L-1300х650-АL | 0.508 м² | 1295 мм | 650 мм | 65 | 1300 мм | саморезы |
| ALW-L-1325х100-АL | 0.080 м² | 1320 мм | 100 мм | 10 | 1325 мм | саморезы |
| ALW-L-1325х125-АL | 0.100 м² | 1320 мм | 125 мм | 13 | 1325 мм | саморезы |
| ALW-L-1325х150-АL | 0.120 м² | 1320 мм | 150 мм | 15 | 1325 мм | саморезы |
| ALW-L-1325х200-АL | 0.159 м² | 1320 мм | 200 мм | 20 | 1325 мм | саморезы |
| ALW-L-1325х225-АL | 0.179 м² | 1320 мм | 225 мм | 23 | 1325 мм | саморезы |
| ALW-L-1325х250-АL | 0.199 м² | 1320 мм | 250 мм | 25 | 1325 мм | саморезы |
| ALW-L-1325х300-АL | 0.239 м² | 1320 мм | 300 мм | 30 | 1325 мм | саморезы |
| ALW-L-1325х325-АL | 0.259 м² | 1320 мм | 325 мм | 33 | 1325 мм | саморезы |
| ALW-L-1325х350-АL | 0.279 м² | 1320 мм | 350 мм | 35 | 1325 мм | саморезы |
| ALW-L-1325х400-АL | 0.319 м² | 1320 мм | 400 мм | 40 | 1325 мм | саморезы |
| ALW-L-1325х425-АL | 0.339 м² | 1320 мм | 425 мм | 43 | 1325 мм | саморезы |
| ALW-L-1325х450-АL | 0.359 м² | 1320 мм | 450 мм | 45 | 1325 мм | саморезы |
| ALW-L-1325х500-АL | 0.399 м² | 1320 мм | 500 мм | 50 | 1325 мм | саморезы |
| ALW-L-1325х525-АL | 0.418 м² | 1320 мм | 525 мм | 53 | 1325 мм | саморезы |
| ALW-L-1325х550-АL | 0.438 м² | 1320 мм | 550 мм | 55 | 1325 мм | саморезы |
| ALW-L-1325х600-АL | 0.478 м² | 1320 мм | 600 мм | 60 | 1325 мм | саморезы |
| ALW-L-1325х625-АL | 0.498 м² | 1320 мм | 625 мм | 63 | 1325 мм | саморезы |
| ALW-L-1325х650-АL | 0.518 м² | 1320 мм | 650 мм | 65 | 1325 мм | саморезы |
| ALW-L-1350х100-АL | 0.081 м² | 1345 мм | 100 мм | 10 | 1350 мм | саморезы |
| ALW-L-1350х125-АL | 0.102 м² | 1345 мм | 125 мм | 13 | 1350 мм | саморезы |
| ALW-L-1350х150-АL | 0.122 м² | 1345 мм | 150 мм | 15 | 1350 мм | саморезы |
| ALW-L-1350х200-АL | 0.162 м² | 1345 мм | 200 мм | 20 | 1350 мм | саморезы |
| ALW-L-1350х225-АL | 0.183 м² | 1345 мм | 225 мм | 23 | 1350 мм | саморезы |
| ALW-L-1350х250-АL | 0.203 м² | 1345 мм | 250 мм | 25 | 1350 мм | саморезы |
| ALW-L-1350х300-АL | 0.244 м² | 1345 мм | 300 мм | 30 | 1350 мм | саморезы |
| ALW-L-1350х325-АL | 0.264 м² | 1345 мм | 325 мм | 33 | 1350 мм | саморезы |
| ALW-L-1350х350-АL | 0.284 м² | 1345 мм | 350 мм | 35 | 1350 мм | саморезы |
| ALW-L-1350х400-АL | 0.325 м² | 1345 мм | 400 мм | 40 | 1350 мм | саморезы |
| ALW-L-1350х425-АL | 0.345 м² | 1345 мм | 425 мм | 43 | 1350 мм | саморезы |
| ALW-L-1350х450-АL | 0.365 м² | 1345 мм | 450 мм | 45 | 1350 мм | саморезы |
| ALW-L-1350х500-АL | 0.406 м² | 1345 мм | 500 мм | 50 | 1350 мм | саморезы |
| ALW-L-1350х525-АL | 0.426 м² | 1345 мм | 525 мм | 53 | 1350 мм | саморезы |
| ALW-L-1350х550-АL | 0.447 м² | 1345 мм | 550 мм | 55 | 1350 мм | саморезы |
| ALW-L-1350х600-АL | 0.487 м² | 1345 мм | 600 мм | 60 | 1350 мм | саморезы |
| ALW-L-1350х625-АL | 0.508 м² | 1345 мм | 625 мм | 63 | 1350 мм | саморезы |
| ALW-L-1350х650-АL | 0.528 м² | 1345 мм | 650 мм | 65 | 1350 мм | саморезы |
| ALW-L-1400х100-АL | 0.084 м² | 1395 мм | 100 мм | 10 | 1400 мм | саморезы |
| ALW-L-1400х125-АL | 0.105 м² | 1395 мм | 125 мм | 13 | 1400 мм | саморезы |
| ALW-L-1400х150-АL | 0.126 м² | 1395 мм | 150 мм | 15 | 1400 мм | саморезы |
| ALW-L-1400х200-АL | 0.168 м² | 1395 мм | 200 мм | 20 | 1400 мм | саморезы |
| ALW-L-1400х225-АL | 0.190 м² | 1395 мм | 225 мм | 23 | 1400 мм | саморезы |
| ALW-L-1400х250-АL | 0.211 м² | 1395 мм | 250 мм | 25 | 1400 мм | саморезы |
| ALW-L-1400х300-АL | 0.253 м² | 1395 мм | 300 мм | 30 | 1400 мм | саморезы |
| ALW-L-1400х325-АL | 0.274 м² | 1395 мм | 325 мм | 33 | 1400 мм | саморезы |
| ALW-L-1400х350-АL | 0.295 м² | 1395 мм | 350 мм | 35 | 1400 мм | саморезы |
| ALW-L-1400х400-АL | 0.337 м² | 1395 мм | 400 мм | 40 | 1400 мм | саморезы |
| ALW-L-1400х425-АL | 0.358 м² | 1395 мм | 425 мм | 43 | 1400 мм | саморезы |
| ALW-L-1400х450-АL | 0.379 м² | 1395 мм | 450 мм | 45 | 1400 мм | саморезы |
| ALW-L-1400х500-АL | 0.421 м² | 1395 мм | 500 мм | 50 | 1400 мм | саморезы |
| ALW-L-1400х525-АL | 0.442 м² | 1395 мм | 525 мм | 53 | 1400 мм | саморезы |
| ALW-L-1400х550-АL | 0.463 м² | 1395 мм | 550 мм | 55 | 1400 мм | саморезы |
| ALW-L-1400х600-АL | 0.505 м² | 1395 мм | 600 мм | 60 | 1400 мм | саморезы |
| ALW-L-1400х625-АL | 0.526 м² | 1395 мм | 625 мм | 63 | 1400 мм | саморезы |
| ALW-L-1400х650-АL | 0.547 м² | 1395 мм | 650 мм | 65 | 1400 мм | саморезы |
| ALW-L-1425х100-АL | 0.086 м² | 1420 мм | 100 мм | 10 | 1425 мм | саморезы |
| ALW-L-1425х125-АL | 0.107 м² | 1420 мм | 125 мм | 13 | 1425 мм | саморезы |
| ALW-L-1425х150-АL | 0.129 м² | 1420 мм | 150 мм | 15 | 1425 мм | саморезы |
| ALW-L-1425х200-АL | 0.171 м² | 1420 мм | 200 мм | 20 | 1425 мм | саморезы |
| ALW-L-1425х225-АL | 0.193 м² | 1420 мм | 225 мм | 23 | 1425 мм | саморезы |
| ALW-L-1425х250-АL | 0.214 м² | 1420 мм | 250 мм | 25 | 1425 мм | саморезы |
| ALW-L-1425х300-АL | 0.257 м² | 1420 мм | 300 мм | 30 | 1425 мм | саморезы |
| ALW-L-1425х325-АL | 0.279 м² | 1420 мм | 325 мм | 33 | 1425 мм | саморезы |
| ALW-L-1425х350-АL | 0.300 м² | 1420 мм | 350 мм | 35 | 1425 мм | саморезы |
| ALW-L-1425х400-АL | 0.343 м² | 1420 мм | 400 мм | 40 | 1425 мм | саморезы |
| ALW-L-1425х425-АL | 0.364 м² | 1420 мм | 425 мм | 43 | 1425 мм | саморезы |
| ALW-L-1425х450-АL | 0.386 м² | 1420 мм | 450 мм | 45 | 1425 мм | саморезы |
| ALW-L-1425х500-АL | 0.429 м² | 1420 мм | 500 мм | 50 | 1425 мм | саморезы |
| ALW-L-1425х525-АL | 0.450 м² | 1420 мм | 525 мм | 53 | 1425 мм | саморезы |
| ALW-L-1425х550-АL | 0.472 м² | 1420 мм | 550 мм | 55 | 1425 мм | саморезы |
| ALW-L-1425х600-АL | 0.514 м² | 1420 мм | 600 мм | 60 | 1425 мм | саморезы |
| ALW-L-1425х625-АL | 0.536 м² | 1420 мм | 625 мм | 63 | 1425 мм | саморезы |
| ALW-L-1425х650-АL | 0.557 м² | 1420 мм | 650 мм | 65 | 1425 мм | саморезы |
| ALW-L-1450х100-АL | 0.087 м² | 1445 мм | 100 мм | 10 | 1450 мм | саморезы |
| ALW-L-1450х125-АL | 0.109 м² | 1445 мм | 125 мм | 13 | 1450 мм | саморезы |
| ALW-L-1450х150-АL | 0.131 м² | 1445 мм | 150 мм | 15 | 1450 мм | саморезы |
| ALW-L-1450х200-АL | 0.174 м² | 1445 мм | 200 мм | 20 | 1450 мм | саморезы |
| ALW-L-1450х225-АL | 0.196 м² | 1445 мм | 225 мм | 23 | 1450 мм | саморезы |
| ALW-L-1450х250-АL | 0.218 м² | 1445 мм | 250 мм | 25 | 1450 мм | саморезы |
| ALW-L-1450х300-АL | 0.262 м² | 1445 мм | 300 мм | 30 | 1450 мм | саморезы |
| ALW-L-1450х325-АL | 0.284 м² | 1445 мм | 325 мм | 33 | 1450 мм | саморезы |
| ALW-L-1450х350-АL | 0.305 м² | 1445 мм | 350 мм | 35 | 1450 мм | саморезы |
| ALW-L-1450х400-АL | 0.349 м² | 1445 мм | 400 мм | 40 | 1450 мм | саморезы |
| ALW-L-1450х425-АL | 0.371 м² | 1445 мм | 425 мм | 43 | 1450 мм | саморезы |
| ALW-L-1450х450-АL | 0.393 м² | 1445 мм | 450 мм | 45 | 1450 мм | саморезы |
| ALW-L-1450х500-АL | 0.436 м² | 1445 мм | 500 мм | 50 | 1450 мм | саморезы |
| ALW-L-1450х525-АL | 0.458 м² | 1445 мм | 525 мм | 53 | 1450 мм | саморезы |
| ALW-L-1450х550-АL | 0.480 м² | 1445 мм | 550 мм | 55 | 1450 мм | саморезы |
| ALW-L-1450х600-АL | 0.523 м² | 1445 мм | 600 мм | 60 | 1450 мм | саморезы |
| ALW-L-1450х625-АL | 0.545 м² | 1445 мм | 625 мм | 63 | 1450 мм | саморезы |
| ALW-L-1450х650-АL | 0.567 м² | 1445 мм | 650 мм | 65 | 1450 мм | саморезы |
| ALW-L-1500х100-АL | 0.090 м² | 1495 мм | 100 мм | 10 | 1500 мм | саморезы |
| ALW-L-1500х125-АL | 0.113 м² | 1495 мм | 125 мм | 13 | 1500 мм | саморезы |
| ALW-L-1500х150-АL | 0.135 м² | 1495 мм | 150 мм | 15 | 1500 мм | саморезы |
| ALW-L-1500х200-АL | 0.180 м² | 1495 мм | 200 мм | 20 | 1500 мм | саморезы |
| ALW-L-1500х225-АL | 0.203 м² | 1495 мм | 225 мм | 23 | 1500 мм | саморезы |
| ALW-L-1500х250-АL | 0.226 м² | 1495 мм | 250 мм | 25 | 1500 мм | саморезы |
| ALW-L-1500х300-АL | 0.271 м² | 1495 мм | 300 мм | 30 | 1500 мм | саморезы |
| ALW-L-1500х325-АL | 0.293 м² | 1495 мм | 325 мм | 33 | 1500 мм | саморезы |
| ALW-L-1500х350-АL | 0.316 м² | 1495 мм | 350 мм | 35 | 1500 мм | саморезы |
| ALW-L-1500х400-АL | 0.361 м² | 1495 мм | 400 мм | 40 | 1500 мм | саморезы |
| ALW-L-1500х425-АL | 0.384 м² | 1495 мм | 425 мм | 43 | 1500 мм | саморезы |
| ALW-L-1500х450-АL | 0.406 м² | 1495 мм | 450 мм | 45 | 1500 мм | саморезы |
| ALW-L-1500х500-АL | 0.451 м² | 1495 мм | 500 мм | 50 | 1500 мм | саморезы |
| ALW-L-1500х525-АL | 0.474 м² | 1495 мм | 525 мм | 53 | 1500 мм | саморезы |
| ALW-L-1500х550-АL | 0.496 м² | 1495 мм | 550 мм | 55 | 1500 мм | саморезы |
| ALW-L-1500х600-АL | 0.541 м² | 1495 мм | 600 мм | 60 | 1500 мм | саморезы |
| ALW-L-1500х625-АL | 0.564 м² | 1495 мм | 625 мм | 63 | 1500 мм | саморезы |
| ALW-L-1500х650-АL | 0.587 м² | 1495 мм | 650 мм | 65 | 1500 мм | саморезы |
| ALW-L-100х100-Z-АА | 0.006 м² | 95 мм | 100 мм | 10 | 100 мм | скрытые защелки |
| ALW-L-125х100-Z-АА | 0.008 м² | 120 мм | 100 мм | 10 | 125 мм | скрытые защелки |
| ALW-L-125х125-Z-АА | 0.009 м² | 120 мм | 125 мм | 13 | 125 мм | скрытые защелки |
| ALW-L-150х100-Z-АА | 0.009 м² | 145 мм | 100 мм | 10 | 150 мм | скрытые защелки |
| ALW-L-150х125-Z-АА | 0.011 м² | 145 мм | 125 мм | 13 | 150 мм | скрытые защелки |
| ALW-L-150х150-Z-АА | 0.014 м² | 145 мм | 150 мм | 15 | 150 мм | скрытые защелки |
| ALW-L-200х100-Z-АА | 0.012 м² | 195 мм | 100 мм | 10 | 200 мм | скрытые защелки |
| ALW-L-200х125-Z-АА | 0.015 м² | 195 мм | 125 мм | 13 | 200 мм | скрытые защелки |
| ALW-L-200х150-Z-АА | 0.018 м² | 195 мм | 150 мм | 15 | 200 мм | скрытые защелки |
| ALW-L-200х200-Z-АА | 0.024 м² | 195 мм | 200 мм | 20 | 200 мм | скрытые защелки |
| ALW-L-225х100-Z-АА | 0.014 м² | 220 мм | 100 мм | 10 | 225 мм | скрытые защелки |
| ALW-L-225х125-Z-АА | 0.017 м² | 220 мм | 125 мм | 13 | 225 мм | скрытые защелки |
| ALW-L-225х150-Z-АА | 0.020 м² | 220 мм | 150 мм | 15 | 225 мм | скрытые защелки |
| ALW-L-225х200-Z-АА | 0.027 м² | 220 мм | 200 мм | 20 | 225 мм | скрытые защелки |
| ALW-L-225х225-Z-АА | 0.030 м² | 220 мм | 225 мм | 23 | 225 мм | скрытые защелки |
| ALW-L-250х100-Z-АА | 0.015 м² | 245 мм | 100 мм | 10 | 250 мм | скрытые защелки |
| ALW-L-250х125-Z-АА | 0.019 м² | 245 мм | 125 мм | 13 | 250 мм | скрытые защелки |
| ALW-L-250х150-Z-АА | 0.023 м² | 245 мм | 150 мм | 15 | 250 мм | скрытые защелки |
| ALW-L-250х200-Z-АА | 0.030 м² | 245 мм | 200 мм | 20 | 250 мм | скрытые защелки |
| ALW-L-250х225-Z-АА | 0.034 м² | 245 мм | 225 мм | 23 | 250 мм | скрытые защелки |
| ALW-L-250х250-Z-АА | 0.038 м² | 245 мм | 250 мм | 25 | 250 мм | скрытые защелки |
| ALW-L-300х100-Z-АА | 0.018 м² | 295 мм | 100 мм | 10 | 300 мм | скрытые защелки |
| ALW-L-300х125-Z-АА | 0.023 м² | 295 мм | 125 мм | 13 | 300 мм | скрытые защелки |
| ALW-L-300х150-Z-АА | 0.027 м² | 295 мм | 150 мм | 15 | 300 мм | скрытые защелки |
| ALW-L-300х200-Z-АА | 0.036 м² | 295 мм | 200 мм | 20 | 300 мм | скрытые защелки |
| ALW-L-300х225-Z-АА | 0.041 м² | 295 мм | 225 мм | 23 | 300 мм | скрытые защелки |
| ALW-L-300х250-Z-АА | 0.045 м² | 295 мм | 250 мм | 25 | 300 мм | скрытые защелки |
| ALW-L-300х300-Z-АА | 0.054 м² | 295 мм | 300 мм | 30 | 300 мм | скрытые защелки |
| ALW-L-325х100-Z-АА | 0.020 м² | 320 мм | 100 мм | 10 | 325 мм | скрытые защелки |
| ALW-L-325х125-Z-АА | 0.024 м² | 320 мм | 125 мм | 13 | 325 мм | скрытые защелки |
| ALW-L-325х150-Z-АА | 0.029 м² | 320 мм | 150 мм | 15 | 325 мм | скрытые защелки |
| ALW-L-325х200-Z-АА | 0.039 м² | 320 мм | 200 мм | 20 | 325 мм | скрытые защелки |
| ALW-L-325х225-Z-АА | 0.044 м² | 320 мм | 225 мм | 23 | 325 мм | скрытые защелки |
| ALW-L-325х250-Z-АА | 0.049 м² | 320 мм | 250 мм | 25 | 325 мм | скрытые защелки |
| ALW-L-325х300-Z-АА | 0.059 м² | 320 мм | 300 мм | 30 | 325 мм | скрытые защелки |
| ALW-L-325х325-Z-АА | 0.064 м² | 320 мм | 325 мм | 33 | 325 мм | скрытые защелки |
| ALW-L-350х100-Z-АА | 0.021 м² | 345 мм | 100 мм | 10 | 350 мм | скрытые защелки |
| ALW-L-350х125-Z-АА | 0.026 м² | 345 мм | 125 мм | 13 | 350 мм | скрытые защелки |
| ALW-L-350х150-Z-АА | 0.032 м² | 345 мм | 150 мм | 15 | 350 мм | скрытые защелки |
| ALW-L-350х200-Z-АА | 0.042 м² | 345 мм | 200 мм | 20 | 350 мм | скрытые защелки |
| ALW-L-350х225-Z-АА | 0.047 м² | 345 мм | 225 мм | 23 | 350 мм | скрытые защелки |
| ALW-L-350х250-Z-АА | 0.053 м² | 345 мм | 250 мм | 25 | 350 мм | скрытые защелки |
| ALW-L-350х300-Z-АА | 0.063 м² | 345 мм | 300 мм | 30 | 350 мм | скрытые защелки |
| ALW-L-350х325-Z-АА | 0.068 м² | 345 мм | 325 мм | 33 | 350 мм | скрытые защелки |
| ALW-L-350х350-Z-АА | 0.074 м² | 345 мм | 350 мм | 35 | 350 мм | скрытые защелки |
| ALW-L-400х100-Z-АА | 0.024 м² | 395 мм | 100 мм | 10 | 400 мм | скрытые защелки |
| ALW-L-400х125-Z-АА | 0.030 м² | 395 мм | 125 мм | 13 | 400 мм | скрытые защелки |
| ALW-L-400х150-Z-АА | 0.036 м² | 395 мм | 150 мм | 15 | 400 мм | скрытые защелки |
| ALW-L-400х200-Z-АА | 0.048 м² | 395 мм | 200 мм | 20 | 400 мм | скрытые защелки |
| ALW-L-400х225-Z-АА | 0.054 м² | 395 мм | 225 мм | 23 | 400 мм | скрытые защелки |
| ALW-L-400х250-Z-АА | 0.060 м² | 395 мм | 250 мм | 25 | 400 мм | скрытые защелки |
| ALW-L-400х300-Z-АА | 0.072 м² | 395 мм | 300 мм | 30 | 400 мм | скрытые защелки |
| ALW-L-400х325-Z-АА | 0.078 м² | 395 мм | 325 мм | 33 | 400 мм | скрытые защелки |
| ALW-L-400х350-Z-АА | 0.084 м² | 395 мм | 350 мм | 35 | 400 мм | скрытые защелки |
| ALW-L-400х400-Z-АА | 0.096 м² | 395 мм | 400 мм | 40 | 400 мм | скрытые защелки |
| ALW-L-425х100-Z-АА | 0.026 м² | 420 мм | 100 мм | 10 | 425 мм | скрытые защелки |
| ALW-L-425х125-Z-АА | 0.032 м² | 420 мм | 125 мм | 13 | 425 мм | скрытые защелки |
| ALW-L-425х150-Z-АА | 0.038 м² | 420 мм | 150 мм | 15 | 425 мм | скрытые защелки |
| ALW-L-425х200-Z-АА | 0.051 м² | 420 мм | 200 мм | 20 | 425 мм | скрытые защелки |
| ALW-L-425х225-Z-АА | 0.058 м² | 420 мм | 225 мм | 23 | 425 мм | скрытые защелки |
| ALW-L-425х250-Z-АА | 0.064 м² | 420 мм | 250 мм | 25 | 425 мм | скрытые защелки |
| ALW-L-425х300-Z-АА | 0.077 м² | 420 мм | 300 мм | 30 | 425 мм | скрытые защелки |
| ALW-L-425х325-Z-АА | 0.083 м² | 420 мм | 325 мм | 33 | 425 мм | скрытые защелки |
| ALW-L-425х350-Z-АА | 0.089 м² | 420 мм | 350 мм | 35 | 425 мм | скрытые защелки |
| ALW-L-425х400-Z-АА | 0.102 м² | 420 мм | 400 мм | 40 | 425 мм | скрытые защелки |
| ALW-L-425х425-Z-АА | 0.109 м² | 420 мм | 425 мм | 43 | 425 мм | скрытые защелки |
| ALW-L-450х100-Z-АА | 0.027 м² | 445 мм | 100 мм | 10 | 450 мм | скрытые защелки |
| ALW-L-450х125-Z-АА | 0.034 м² | 445 мм | 125 мм | 13 | 450 мм | скрытые защелки |
| ALW-L-450х150-Z-АА | 0.041 м² | 445 мм | 150 мм | 15 | 450 мм | скрытые защелки |
| ALW-L-450х200-Z-АА | 0.054 м² | 445 мм | 200 мм | 20 | 450 мм | скрытые защелки |
| ALW-L-450х225-Z-АА | 0.061 м² | 445 мм | 225 мм | 23 | 450 мм | скрытые защелки |
| ALW-L-450х250-Z-АА | 0.068 м² | 445 мм | 250 мм | 25 | 450 мм | скрытые защелки |
| ALW-L-450х300-Z-АА | 0.081 м² | 445 мм | 300 мм | 30 | 450 мм | скрытые защелки |
| ALW-L-450х325-Z-АА | 0.088 м² | 445 мм | 325 мм | 33 | 450 мм | скрытые защелки |
| ALW-L-450х350-Z-АА | 0.095 м² | 445 мм | 350 мм | 35 | 450 мм | скрытые защелки |
| ALW-L-450х400-Z-АА | 0.108 м² | 445 мм | 400 мм | 40 | 450 мм | скрытые защелки |
| ALW-L-450х425-Z-АА | 0.115 м² | 445 мм | 425 мм | 43 | 450 мм | скрытые защелки |
| ALW-L-450х450-Z-АА | 0.122 м² | 445 мм | 450 мм | 45 | 450 мм | скрытые защелки |
| ALW-L-500х100-Z-АА | 0.030 м² | 495 мм | 100 мм | 10 | 500 мм | скрытые защелки |
| ALW-L-500х125-Z-АА | 0.038 м² | 495 мм | 125 мм | 13 | 500 мм | скрытые защелки |
| ALW-L-500х150-Z-АА | 0.045 м² | 495 мм | 150 мм | 15 | 500 мм | скрытые защелки |
| ALW-L-500х200-Z-АА | 0.060 м² | 495 мм | 200 мм | 20 | 500 мм | скрытые защелки |
| ALW-L-500х225-Z-АА | 0.068 м² | 495 мм | 225 мм | 23 | 500 мм | скрытые защелки |
| ALW-L-500х250-Z-АА | 0.075 м² | 495 мм | 250 мм | 25 | 500 мм | скрытые защелки |
| ALW-L-500х300-Z-АА | 0.090 м² | 495 мм | 300 мм | 30 | 500 мм | скрытые защелки |
| ALW-L-500х325-Z-АА | 0.098 м² | 495 мм | 325 мм | 33 | 500 мм | скрытые защелки |
| ALW-L-500х350-Z-АА | 0.105 м² | 495 мм | 350 мм | 35 | 500 мм | скрытые защелки |
| ALW-L-500х400-Z-АА | 0.120 м² | 495 мм | 400 мм | 40 | 500 мм | скрытые защелки |
| ALW-L-500х425-Z-АА | 0.128 м² | 495 мм | 425 мм | 43 | 500 мм | скрытые защелки |
| ALW-L-500х450-Z-АА | 0.135 м² | 495 мм | 450 мм | 45 | 500 мм | скрытые защелки |
| ALW-L-500х500-Z-АА | 0.150 м² | 495 мм | 500 мм | 50 | 500 мм | скрытые защелки |
| ALW-L-525х100-Z-АА | 0.032 м² | 520 мм | 100 мм | 10 | 525 мм | скрытые защелки |
| ALW-L-525х125-Z-АА | 0.039 м² | 520 мм | 125 мм | 13 | 525 мм | скрытые защелки |
| ALW-L-525х150-Z-АА | 0.047 м² | 520 мм | 150 мм | 15 | 525 мм | скрытые защелки |
| ALW-L-525х200-Z-АА | 0.063 м² | 520 мм | 200 мм | 20 | 525 мм | скрытые защелки |
| ALW-L-525х225-Z-АА | 0.071 м² | 520 мм | 225 мм | 23 | 525 мм | скрытые защелки |
| ALW-L-525х250-Z-АА | 0.079 м² | 520 мм | 250 мм | 25 | 525 мм | скрытые защелки |
| ALW-L-525х300-Z-АА | 0.095 м² | 520 мм | 300 мм | 30 | 525 мм | скрытые защелки |
| ALW-L-525х325-Z-АА | 0.103 м² | 520 мм | 325 мм | 33 | 525 мм | скрытые защелки |
| ALW-L-525х350-Z-АА | 0.111 м² | 520 мм | 350 мм | 35 | 525 мм | скрытые защелки |
| ALW-L-525х400-Z-АА | 0.126 м² | 520 мм | 400 мм | 40 | 525 мм | скрытые защелки |
| ALW-L-525х425-Z-АА | 0.134 м² | 520 мм | 425 мм | 43 | 525 мм | скрытые защелки |
| ALW-L-525х450-Z-АА | 0.142 м² | 520 мм | 450 мм | 45 | 525 мм | скрытые защелки |
| ALW-L-525х500-Z-АА | 0.158 м² | 520 мм | 500 мм | 50 | 525 мм | скрытые защелки |
| ALW-L-525х525-Z-АА | 0.166 м² | 520 мм | 525 мм | 53 | 525 мм | скрытые защелки |
| ALW-L-550х100-Z-АА | 0.033 м² | 545 мм | 100 мм | 10 | 550 мм | скрытые защелки |
| ALW-L-550х125-Z-АА | 0.041 м² | 545 мм | 125 мм | 13 | 550 мм | скрытые защелки |
| ALW-L-550х150-Z-АА | 0.050 м² | 545 мм | 150 мм | 15 | 550 мм | скрытые защелки |
| ALW-L-550х200-Z-АА | 0.066 м² | 545 мм | 200 мм | 20 | 550 мм | скрытые защелки |
| ALW-L-550х225-Z-АА | 0.074 м² | 545 мм | 225 мм | 23 | 550 мм | скрытые защелки |
| ALW-L-550х250-Z-АА | 0.083 м² | 545 мм | 250 мм | 25 | 550 мм | скрытые защелки |
| ALW-L-550х300-Z-АА | 0.099 м² | 545 мм | 300 мм | 30 | 550 мм | скрытые защелки |
| ALW-L-550х325-Z-АА | 0.108 м² | 545 мм | 325 мм | 33 | 550 мм | скрытые защелки |
| ALW-L-550х350-Z-АА | 0.116 м² | 545 мм | 350 мм | 35 | 550 мм | скрытые защелки |
| ALW-L-550х400-Z-АА | 0.132 м² | 545 мм | 400 мм | 40 | 550 мм | скрытые защелки |
| ALW-L-550х425-Z-АА | 0.141 м² | 545 мм | 425 мм | 43 | 550 мм | скрытые защелки |
| ALW-L-550х450-Z-АА | 0.149 м² | 545 мм | 450 мм | 45 | 550 мм | скрытые защелки |
| ALW-L-550х500-Z-АА | 0.165 м² | 545 мм | 500 мм | 50 | 550 мм | скрытые защелки |
| ALW-L-550х525-Z-АА | 0.174 м² | 545 мм | 525 мм | 53 | 550 мм | скрытые защелки |
| ALW-L-550х550-Z-АА | 0.182 м² | 545 мм | 550 мм | 55 | 550 мм | скрытые защелки |
| ALW-L-600х100-Z-АА | 0.036 м² | 595 мм | 100 мм | 10 | 600 мм | скрытые защелки |
| ALW-L-600х125-Z-АА | 0.045 м² | 595 мм | 125 мм | 13 | 600 мм | скрытые защелки |
| ALW-L-600х150-Z-АА | 0.054 м² | 595 мм | 150 мм | 15 | 600 мм | скрытые защелки |
| ALW-L-600х200-Z-АА | 0.072 м² | 595 мм | 200 мм | 20 | 600 мм | скрытые защелки |
| ALW-L-600х225-Z-АА | 0.081 м² | 595 мм | 225 мм | 23 | 600 мм | скрытые защелки |
| ALW-L-600х250-Z-АА | 0.090 м² | 595 мм | 250 мм | 25 | 600 мм | скрытые защелки |
| ALW-L-600х300-Z-АА | 0.108 м² | 595 мм | 300 мм | 30 | 600 мм | скрытые защелки |
| ALW-L-600х325-Z-АА | 0.117 м² | 595 мм | 325 мм | 33 | 600 мм | скрытые защелки |
| ALW-L-600х350-Z-АА | 0.126 м² | 595 мм | 350 мм | 35 | 600 мм | скрытые защелки |
| ALW-L-600х400-Z-АА | 0.144 м² | 595 мм | 400 мм | 40 | 600 мм | скрытые защелки |
| ALW-L-600х425-Z-АА | 0.153 м² | 595 мм | 425 мм | 43 | 600 мм | скрытые защелки |
| ALW-L-600х450-Z-АА | 0.162 м² | 595 мм | 450 мм | 45 | 600 мм | скрытые защелки |
| ALW-L-600х500-Z-АА | 0.180 м² | 595 мм | 500 мм | 50 | 600 мм | скрытые защелки |
| ALW-L-600х525-Z-АА | 0.190 м² | 595 мм | 525 мм | 53 | 600 мм | скрытые защелки |
| ALW-L-600х550-Z-АА | 0.199 м² | 595 мм | 550 мм | 55 | 600 мм | скрытые защелки |
| ALW-L-600х600-Z-АА | 0.217 м² | 595 мм | 600 мм | 60 | 600 мм | скрытые защелки |
| ALW-L-625х100-Z-АА | 0.038 м² | 620 мм | 100 мм | 10 | 625 мм | скрытые защелки |
| ALW-L-625х125-Z-АА | 0.047 м² | 620 мм | 125 мм | 13 | 625 мм | скрытые защелки |
| ALW-L-625х150-Z-АА | 0.056 м² | 620 мм | 150 мм | 15 | 625 мм | скрытые защелки |
| ALW-L-625х200-Z-АА | 0.075 м² | 620 мм | 200 мм | 20 | 625 мм | скрытые защелки |
| ALW-L-625х225-Z-АА | 0.085 м² | 620 мм | 225 мм | 23 | 625 мм | скрытые защелки |
| ALW-L-625х250-Z-АА | 0.094 м² | 620 мм | 250 мм | 25 | 625 мм | скрытые защелки |
| ALW-L-625х300-Z-АА | 0.113 м² | 620 мм | 300 мм | 30 | 625 мм | скрытые защелки |
| ALW-L-625х325-Z-АА | 0.122 м² | 620 мм | 325 мм | 33 | 625 мм | скрытые защелки |
| ALW-L-625х350-Z-АА | 0.132 м² | 620 мм | 350 мм | 35 | 625 мм | скрытые защелки |
| ALW-L-625х400-Z-АА | 0.150 м² | 620 мм | 400 мм | 40 | 625 мм | скрытые защелки |
| ALW-L-625х425-Z-АА | 0.160 м² | 620 мм | 425 мм | 43 | 625 мм | скрытые защелки |
| ALW-L-625х450-Z-АА | 0.169 м² | 620 мм | 450 мм | 45 | 625 мм | скрытые защелки |
| ALW-L-625х500-Z-АА | 0.188 м² | 620 мм | 500 мм | 50 | 625 мм | скрытые защелки |
| ALW-L-625х525-Z-АА | 0.197 м² | 620 мм | 525 мм | 53 | 625 мм | скрытые защелки |
| ALW-L-625х550-Z-АА | 0.207 м² | 620 мм | 550 мм | 55 | 625 мм | скрытые защелки |
| ALW-L-625х600-Z-АА | 0.226 м² | 620 мм | 600 мм | 60 | 625 мм | скрытые защелки |
| ALW-L-625х625-Z-АА | 0.235 м² | 620 мм | 625 мм | 63 | 625 мм | скрытые защелки |
| ALW-L-650х100-Z-АА | 0.039 м² | 645 мм | 100 мм | 10 | 650 мм | скрытые защелки |
| ALW-L-650х125-Z-АА | 0.049 м² | 645 мм | 125 мм | 13 | 650 мм | скрытые защелки |
| ALW-L-650х150-Z-АА | 0.059 м² | 645 мм | 150 мм | 15 | 650 мм | скрытые защелки |
| ALW-L-650х200-Z-АА | 0.078 м² | 645 мм | 200 мм | 20 | 650 мм | скрытые защелки |
| ALW-L-650х225-Z-АА | 0.088 м² | 645 мм | 225 мм | 23 | 650 мм | скрытые защелки |
| ALW-L-650х250-Z-АА | 0.098 м² | 645 мм | 250 мм | 25 | 650 мм | скрытые защелки |
| ALW-L-650х300-Z-АА | 0.117 м² | 645 мм | 300 мм | 30 | 650 мм | скрытые защелки |
| ALW-L-650х325-Z-АА | 0.127 м² | 645 мм | 325 мм | 33 | 650 мм | скрытые защелки |
| ALW-L-650х350-Z-АА | 0.137 м² | 645 мм | 350 мм | 35 | 650 мм | скрытые защелки |
| ALW-L-650х400-Z-АА | 0.156 м² | 645 мм | 400 мм | 40 | 650 мм | скрытые защелки |
| ALW-L-650х425-Z-АА | 0.166 м² | 645 мм | 425 мм | 43 | 650 мм | скрытые защелки |
| ALW-L-650х450-Z-АА | 0.176 м² | 645 мм | 450 мм | 45 | 650 мм | скрытые защелки |
| ALW-L-650х500-Z-АА | 0.196 м² | 645 мм | 500 мм | 50 | 650 мм | скрытые защелки |
| ALW-L-650х525-Z-АА | 0.205 м² | 645 мм | 525 мм | 53 | 650 мм | скрытые защелки |
| ALW-L-650х550-Z-АА | 0.215 м² | 645 мм | 550 мм | 55 | 650 мм | скрытые защелки |
| ALW-L-650х600-Z-АА | 0.235 м² | 645 мм | 600 мм | 60 | 650 мм | скрытые защелки |
| ALW-L-650х625-Z-АА | 0.244 м² | 645 мм | 625 мм | 63 | 650 мм | скрытые защелки |
| ALW-L-650х650-Z-АА | 0.254 м² | 645 мм | 650 мм | 65 | 650 мм | скрытые защелки |
| ALW-L-700х100-Z-АА | 0.042 м² | 695 мм | 100 мм | 10 | 700 мм | скрытые защелки |
| ALW-L-700х125-Z-АА | 0.053 м² | 695 мм | 125 мм | 13 | 700 мм | скрытые защелки |
| ALW-L-700х150-Z-АА | 0.063 м² | 695 мм | 150 мм | 15 | 700 мм | скрытые защелки |
| ALW-L-700х200-Z-АА | 0.084 м² | 695 мм | 200 мм | 20 | 700 мм | скрытые защелки |
| ALW-L-700х225-Z-АА | 0.095 м² | 695 мм | 225 мм | 23 | 700 мм | скрытые защелки |
| ALW-L-700х250-Z-АА | 0.105 м² | 695 мм | 250 мм | 25 | 700 мм | скрытые защелки |
| ALW-L-700х300-Z-АА | 0.126 м² | 695 мм | 300 мм | 30 | 700 мм | скрытые защелки |
| ALW-L-700х325-Z-АА | 0.137 м² | 695 мм | 325 мм | 33 | 700 мм | скрытые защелки |
| ALW-L-700х350-Z-АА | 0.147 м² | 695 мм | 350 мм | 35 | 700 мм | скрытые защелки |
| ALW-L-700х400-Z-АА | 0.168 м² | 695 мм | 400 мм | 40 | 700 мм | скрытые защелки |
| ALW-L-700х425-Z-АА | 0.179 м² | 695 мм | 425 мм | 43 | 700 мм | скрытые защелки |
| ALW-L-700х450-Z-АА | 0.190 м² | 695 мм | 450 мм | 45 | 700 мм | скрытые защелки |
| ALW-L-700х500-Z-АА | 0.211 м² | 695 мм | 500 мм | 50 | 700 мм | скрытые защелки |
| ALW-L-700х525-Z-АА | 0.221 м² | 695 мм | 525 мм | 53 | 700 мм | скрытые защелки |
| ALW-L-700х550-Z-АА | 0.232 м² | 695 мм | 550 мм | 55 | 700 мм | скрытые защелки |
| ALW-L-700х600-Z-АА | 0.253 м² | 695 мм | 600 мм | 60 | 700 мм | скрытые защелки |
| ALW-L-700х625-Z-АА | 0.263 м² | 695 мм | 625 мм | 63 | 700 мм | скрытые защелки |
| ALW-L-700х650-Z-АА | 0.274 м² | 695 мм | 650 мм | 65 | 700 мм | скрытые защелки |
| ALW-L-725х100-Z-АА | 0.044 м² | 720 мм | 100 мм | 10 | 725 мм | скрытые защелки |
| ALW-L-725х125-Z-АА | 0.055 м² | 720 мм | 125 мм | 13 | 725 мм | скрытые защелки |
| ALW-L-725х150-Z-АА | 0.065 м² | 720 мм | 150 мм | 15 | 725 мм | скрытые защелки |
| ALW-L-725х200-Z-АА | 0.087 м² | 720 мм | 200 мм | 20 | 725 мм | скрытые защелки |
| ALW-L-725х225-Z-АА | 0.098 м² | 720 мм | 225 мм | 23 | 725 мм | скрытые защелки |
| ALW-L-725х250-Z-АА | 0.109 м² | 720 мм | 250 мм | 25 | 725 мм | скрытые защелки |
| ALW-L-725х300-Z-АА | 0.131 м² | 720 мм | 300 мм | 30 | 725 мм | скрытые защелки |
| ALW-L-725х325-Z-АА | 0.142 м² | 720 мм | 325 мм | 33 | 725 мм | скрытые защелки |
| ALW-L-725х350-Z-АА | 0.153 м² | 720 мм | 350 мм | 35 | 725 мм | скрытые защелки |
| ALW-L-725х400-Z-АА | 0.174 м² | 720 мм | 400 мм | 40 | 725 мм | скрытые защелки |
| ALW-L-725х425-Z-АА | 0.185 м² | 720 мм | 425 мм | 43 | 725 мм | скрытые защелки |
| ALW-L-725х450-Z-АА | 0.196 м² | 720 мм | 450 мм | 45 | 725 мм | скрытые защелки |
| ALW-L-725х500-Z-АА | 0.218 м² | 720 мм | 500 мм | 50 | 725 мм | скрытые защелки |
| ALW-L-725х525-Z-АА | 0.229 м² | 720 мм | 525 мм | 53 | 725 мм | скрытые защелки |
| ALW-L-725х550-Z-АА | 0.240 м² | 720 мм | 550 мм | 55 | 725 мм | скрытые защелки |
| ALW-L-725х600-Z-АА | 0.262 м² | 720 мм | 600 мм | 60 | 725 мм | скрытые защелки |
| ALW-L-725х625-Z-АА | 0.273 м² | 720 мм | 625 мм | 63 | 725 мм | скрытые защелки |
| ALW-L-725х650-Z-АА | 0.284 м² | 720 мм | 650 мм | 65 | 725 мм | скрытые защелки |
| ALW-L-750х100-Z-АА | 0.045 м² | 745 мм | 100 мм | 10 | 750 мм | скрытые защелки |
| ALW-L-750х125-Z-АА | 0.056 м² | 745 мм | 125 мм | 13 | 750 мм | скрытые защелки |
| ALW-L-750х150-Z-АА | 0.068 м² | 745 мм | 150 мм | 15 | 750 мм | скрытые защелки |
| ALW-L-750х200-Z-АА | 0.090 м² | 745 мм | 200 мм | 20 | 750 мм | скрытые защелки |
| ALW-L-750х225-Z-АА | 0.102 м² | 745 мм | 225 мм | 23 | 750 мм | скрытые защелки |
| ALW-L-750х250-Z-АА | 0.113 м² | 745 мм | 250 мм | 25 | 750 мм | скрытые защелки |
| ALW-L-750х300-Z-АА | 0.135 м² | 745 мм | 300 мм | 30 | 750 мм | скрытые защелки |
| ALW-L-750х325-Z-АА | 0.147 м² | 745 мм | 325 мм | 33 | 750 мм | скрытые защелки |
| ALW-L-750х350-Z-АА | 0.158 м² | 745 мм | 350 мм | 35 | 750 мм | скрытые защелки |
| ALW-L-750х400-Z-АА | 0.180 м² | 745 мм | 400 мм | 40 | 750 мм | скрытые защелки |
| ALW-L-750х425-Z-АА | 0.192 м² | 745 мм | 425 мм | 43 | 750 мм | скрытые защелки |
| ALW-L-750х450-Z-АА | 0.203 м² | 745 мм | 450 мм | 45 | 750 мм | скрытые защелки |
| ALW-L-750х500-Z-АА | 0.226 м² | 745 мм | 500 мм | 50 | 750 мм | скрытые защелки |
| ALW-L-750х525-Z-АА | 0.237 м² | 745 мм | 525 мм | 53 | 750 мм | скрытые защелки |
| ALW-L-750х550-Z-АА | 0.248 м² | 745 мм | 550 мм | 55 | 750 мм | скрытые защелки |
| ALW-L-750х600-Z-АА | 0.271 м² | 745 мм | 600 мм | 60 | 750 мм | скрытые защелки |
| ALW-L-750х625-Z-АА | 0.282 м² | 745 мм | 625 мм | 63 | 750 мм | скрытые защелки |
| ALW-L-750х650-Z-АА | 0.293 м² | 745 мм | 650 мм | 65 | 750 мм | скрытые защелки |
| ALW-L-800х100-Z-АА | 0.048 м² | 795 мм | 100 мм | 10 | 800 мм | скрытые защелки |
| ALW-L-800х125-Z-АА | 0.060 м² | 795 мм | 125 мм | 13 | 800 мм | скрытые защелки |
| ALW-L-800х150-Z-АА | 0.072 м² | 795 мм | 150 мм | 15 | 800 мм | скрытые защелки |
| ALW-L-800х200-Z-АА | 0.096 м² | 795 мм | 200 мм | 20 | 800 мм | скрытые защелки |
| ALW-L-800х225-Z-АА | 0.108 м² | 795 мм | 225 мм | 23 | 800 мм | скрытые защелки |
| ALW-L-800х250-Z-АА | 0.120 м² | 795 мм | 250 мм | 25 | 800 мм | скрытые защелки |
| ALW-L-800х300-Z-АА | 0.144 м² | 795 мм | 300 мм | 30 | 800 мм | скрытые защелки |
| ALW-L-800х325-Z-АА | 0.156 м² | 795 мм | 325 мм | 33 | 800 мм | скрытые защелки |
| ALW-L-800х350-Z-АА | 0.168 м² | 795 мм | 350 мм | 35 | 800 мм | скрытые защелки |
| ALW-L-800х400-Z-АА | 0.193 м² | 795 мм | 400 мм | 40 | 800 мм | скрытые защелки |
| ALW-L-800х425-Z-АА | 0.205 м² | 795 мм | 425 мм | 43 | 800 мм | скрытые защелки |
| ALW-L-800х450-Z-АА | 0.217 м² | 795 мм | 450 мм | 45 | 800 мм | скрытые защелки |
| ALW-L-800х500-Z-АА | 0.241 м² | 795 мм | 500 мм | 50 | 800 мм | скрытые защелки |
| ALW-L-800х525-Z-АА | 0.253 м² | 795 мм | 525 мм | 53 | 800 мм | скрытые защелки |
| ALW-L-800х550-Z-АА | 0.265 м² | 795 мм | 550 мм | 55 | 800 мм | скрытые защелки |
| ALW-L-800х600-Z-АА | 0.289 м² | 795 мм | 600 мм | 60 | 800 мм | скрытые защелки |
| ALW-L-800х625-Z-АА | 0.301 м² | 795 мм | 625 мм | 63 | 800 мм | скрытые защелки |
| ALW-L-800х650-Z-АА | 0.313 м² | 795 мм | 650 мм | 65 | 800 мм | скрытые защелки |
| ALW-L-825х100-Z-АА | 0.050 м² | 820 мм | 100 мм | 10 | 825 мм | скрытые защелки |
| ALW-L-825х125-Z-АА | 0.062 м² | 820 мм | 125 мм | 13 | 825 мм | скрытые защелки |
| ALW-L-825х150-Z-АА | 0.074 м² | 820 мм | 150 мм | 15 | 825 мм | скрытые защелки |
| ALW-L-825х200-Z-АА | 0.099 м² | 820 мм | 200 мм | 20 | 825 мм | скрытые защелки |
| ALW-L-825х225-Z-АА | 0.112 м² | 820 мм | 225 мм | 23 | 825 мм | скрытые защелки |
| ALW-L-825х250-Z-АА | 0.124 м² | 820 мм | 250 мм | 25 | 825 мм | скрытые защелки |
| ALW-L-825х300-Z-АА | 0.149 м² | 820 мм | 300 мм | 30 | 825 мм | скрытые защелки |
| ALW-L-825х325-Z-АА | 0.161 м² | 820 мм | 325 мм | 33 | 825 мм | скрытые защелки |
| ALW-L-825х350-Z-АА | 0.174 м² | 820 мм | 350 мм | 35 | 825 мм | скрытые защелки |
| ALW-L-825х400-Z-АА | 0.199 м² | 820 мм | 400 мм | 40 | 825 мм | скрытые защелки |
| ALW-L-825х425-Z-АА | 0.211 м² | 820 мм | 425 мм | 43 | 825 мм | скрытые защелки |
| ALW-L-825х450-Z-АА | 0.223 м² | 820 мм | 450 мм | 45 | 825 мм | скрытые защелки |
| ALW-L-825х500-Z-АА | 0.248 м² | 820 мм | 500 мм | 50 | 825 мм | скрытые защелки |
| ALW-L-825х525-Z-АА | 0.261 м² | 820 мм | 525 мм | 53 | 825 мм | скрытые защелки |
| ALW-L-825х550-Z-АА | 0.273 м² | 820 мм | 550 мм | 55 | 825 мм | скрытые защелки |
| ALW-L-825х600-Z-АА | 0.298 м² | 820 мм | 600 мм | 60 | 825 мм | скрытые защелки |
| ALW-L-825х625-Z-АА | 0.310 м² | 820 мм | 625 мм | 63 | 825 мм | скрытые защелки |
| ALW-L-825х650-Z-АА | 0.323 м² | 820 мм | 650 мм | 65 | 825 мм | скрытые защелки |
| ALW-L-850х100-Z-АА | 0.051 м² | 845 мм | 100 мм | 10 | 850 мм | скрытые защелки |
| ALW-L-850х125-Z-АА | 0.064 м² | 845 мм | 125 мм | 13 | 850 мм | скрытые защелки |
| ALW-L-850х150-Z-АА | 0.077 м² | 845 мм | 150 мм | 15 | 850 мм | скрытые защелки |
| ALW-L-850х200-Z-АА | 0.102 м² | 845 мм | 200 мм | 20 | 850 мм | скрытые защелки |
| ALW-L-850х225-Z-АА | 0.115 м² | 845 мм | 225 мм | 23 | 850 мм | скрытые защелки |
| ALW-L-850х250-Z-АА | 0.128 м² | 845 мм | 250 мм | 25 | 850 мм | скрытые защелки |
| ALW-L-850х300-Z-АА | 0.153 м² | 845 мм | 300 мм | 30 | 850 мм | скрытые защелки |
| ALW-L-850х325-Z-АА | 0.166 м² | 845 мм | 325 мм | 33 | 850 мм | скрытые защелки |
| ALW-L-850х350-Z-АА | 0.179 м² | 845 мм | 350 мм | 35 | 850 мм | скрытые защелки |
| ALW-L-850х400-Z-АА | 0.205 м² | 845 мм | 400 мм | 40 | 850 мм | скрытые защелки |
| ALW-L-850х425-Z-АА | 0.217 м² | 845 мм | 425 мм | 43 | 850 мм | скрытые защелки |
| ALW-L-850х450-Z-АА | 0.230 м² | 845 мм | 450 мм | 45 | 850 мм | скрытые защелки |
| ALW-L-850х500-Z-АА | 0.256 м² | 845 мм | 500 мм | 50 | 850 мм | скрытые защелки |
| ALW-L-850х525-Z-АА | 0.268 м² | 845 мм | 525 мм | 53 | 850 мм | скрытые защелки |
| ALW-L-850х550-Z-АА | 0.281 м² | 845 мм | 550 мм | 55 | 850 мм | скрытые защелки |
| ALW-L-850х600-Z-АА | 0.307 м² | 845 мм | 600 мм | 60 | 850 мм | скрытые защелки |
| ALW-L-850х625-Z-АА | 0.320 м² | 845 мм | 625 мм | 63 | 850 мм | скрытые защелки |
| ALW-L-850х650-Z-АА | 0.332 м² | 845 мм | 650 мм | 65 | 850 мм | скрытые защелки |
| ALW-L-900х100-Z-АА | 0.054 м² | 895 мм | 100 мм | 10 | 900 мм | скрытые защелки |
| ALW-L-900х125-Z-АА | 0.068 м² | 895 мм | 125 мм | 13 | 900 мм | скрытые защелки |
| ALW-L-900х150-Z-АА | 0.081 м² | 895 мм | 150 мм | 15 | 900 мм | скрытые защелки |
| ALW-L-900х200-Z-АА | 0.108 м² | 895 мм | 200 мм | 20 | 900 мм | скрытые защелки |
| ALW-L-900х225-Z-АА | 0.122 м² | 895 мм | 225 мм | 23 | 900 мм | скрытые защелки |
| ALW-L-900х250-Z-АА | 0.135 м² | 895 мм | 250 мм | 25 | 900 мм | скрытые защелки |
| ALW-L-900х300-Z-АА | 0.162 м² | 895 мм | 300 мм | 30 | 900 мм | скрытые защелки |
| ALW-L-900х325-Z-АА | 0.176 м² | 895 мм | 325 мм | 33 | 900 мм | скрытые защелки |
| ALW-L-900х350-Z-АА | 0.190 м² | 895 мм | 350 мм | 35 | 900 мм | скрытые защелки |
| ALW-L-900х400-Z-АА | 0.217 м² | 895 мм | 400 мм | 40 | 900 мм | скрытые защелки |
| ALW-L-900х425-Z-АА | 0.230 м² | 895 мм | 425 мм | 43 | 900 мм | скрытые защелки |
| ALW-L-900х450-Z-АА | 0.244 м² | 895 мм | 450 мм | 45 | 900 мм | скрытые защелки |
| ALW-L-900х500-Z-АА | 0.271 м² | 895 мм | 500 мм | 50 | 900 мм | скрытые защелки |
| ALW-L-900х525-Z-АА | 0.284 м² | 895 мм | 525 мм | 53 | 900 мм | скрытые защелки |
| ALW-L-900х550-Z-АА | 0.298 м² | 895 мм | 550 мм | 55 | 900 мм | скрытые защелки |
| ALW-L-900х600-Z-АА | 0.325 м² | 895 мм | 600 мм | 60 | 900 мм | скрытые защелки |
| ALW-L-900х625-Z-АА | 0.338 м² | 895 мм | 625 мм | 63 | 900 мм | скрытые защелки |
| ALW-L-900х650-Z-АА | 0.352 м² | 895 мм | 650 мм | 65 | 900 мм | скрытые защелки |
| ALW-L-925х100-Z-АА | 0.056 м² | 920 мм | 100 мм | 10 | 925 мм | скрытые защелки |
| ALW-L-925х125-Z-АА | 0.070 м² | 920 мм | 125 мм | 13 | 925 мм | скрытые защелки |
| ALW-L-925х150-Z-АА | 0.083 м² | 920 мм | 150 мм | 15 | 925 мм | скрытые защелки |
| ALW-L-925х200-Z-АА | 0.111 м² | 920 мм | 200 мм | 20 | 925 мм | скрытые защелки |
| ALW-L-925х225-Z-АА | 0.125 м² | 920 мм | 225 мм | 23 | 925 мм | скрытые защелки |
| ALW-L-925х250-Z-АА | 0.139 м² | 920 мм | 250 мм | 25 | 925 мм | скрытые защелки |
| ALW-L-925х300-Z-АА | 0.167 м² | 920 мм | 300 мм | 30 | 925 мм | скрытые защелки |
| ALW-L-925х325-Z-АА | 0.181 м² | 920 мм | 325 мм | 33 | 925 мм | скрытые защелки |
| ALW-L-925х350-Z-АА | 0.195 м² | 920 мм | 350 мм | 35 | 925 мм | скрытые защелки |
| ALW-L-925х400-Z-АА | 0.223 м² | 920 мм | 400 мм | 40 | 925 мм | скрытые защелки |
| ALW-L-925х425-Z-АА | 0.237 м² | 920 мм | 425 мм | 43 | 925 мм | скрытые защелки |
| ALW-L-925х450-Z-АА | 0.250 м² | 920 мм | 450 мм | 45 | 925 мм | скрытые защелки |
| ALW-L-925х500-Z-АА | 0.278 м² | 920 мм | 500 мм | 50 | 925 мм | скрытые защелки |
| ALW-L-925х525-Z-АА | 0.292 м² | 920 мм | 525 мм | 53 | 925 мм | скрытые защелки |
| ALW-L-925х550-Z-АА | 0.306 м² | 920 мм | 550 мм | 55 | 925 мм | скрытые защелки |
| ALW-L-925х600-Z-АА | 0.334 м² | 920 мм | 600 мм | 60 | 925 мм | скрытые защелки |
| ALW-L-925х625-Z-АА | 0.348 м² | 920 мм | 625 мм | 63 | 925 мм | скрытые защелки |
| ALW-L-925х650-Z-АА | 0.362 м² | 920 мм | 650 мм | 65 | 925 мм | скрытые защелки |
| ALW-L-950х100-Z-АА | 0.057 м² | 945 мм | 100 мм | 10 | 950 мм | скрытые защелки |
| ALW-L-950х125-Z-АА | 0.071 м² | 945 мм | 125 мм | 13 | 950 мм | скрытые защелки |
| ALW-L-950х150-Z-АА | 0.086 м² | 945 мм | 150 мм | 15 | 950 мм | скрытые защелки |
| ALW-L-950х200-Z-АА | 0.114 м² | 945 мм | 200 мм | 20 | 950 мм | скрытые защелки |
| ALW-L-950х225-Z-АА | 0.129 м² | 945 мм | 225 мм | 23 | 950 мм | скрытые защелки |
| ALW-L-950х250-Z-АА | 0.143 м² | 945 мм | 250 мм | 25 | 950 мм | скрытые защелки |
| ALW-L-950х300-Z-АА | 0.171 м² | 945 мм | 300 мм | 30 | 950 мм | скрытые защелки |
| ALW-L-950х325-Z-АА | 0.186 м² | 945 мм | 325 мм | 33 | 950 мм | скрытые защелки |
| ALW-L-950х350-Z-АА | 0.200 м² | 945 мм | 350 мм | 35 | 950 мм | скрытые защелки |
| ALW-L-950х400-Z-АА | 0.229 м² | 945 мм | 400 мм | 40 | 950 мм | скрытые защелки |
| ALW-L-950х425-Z-АА | 0.243 м² | 945 мм | 425 мм | 43 | 950 мм | скрытые защелки |
| ALW-L-950х450-Z-АА | 0.257 м² | 945 мм | 450 мм | 45 | 950 мм | скрытые защелки |
| ALW-L-950х500-Z-АА | 0.286 м² | 945 мм | 500 мм | 50 | 950 мм | скрытые защелки |
| ALW-L-950х525-Z-АА | 0.300 м² | 945 мм | 525 мм | 53 | 950 мм | скрытые защелки |
| ALW-L-950х550-Z-АА | 0.314 м² | 945 мм | 550 мм | 55 | 950 мм | скрытые защелки |
| ALW-L-950х600-Z-АА | 0.343 м² | 945 мм | 600 мм | 60 | 950 мм | скрытые защелки |
| ALW-L-950х625-Z-АА | 0.357 м² | 945 мм | 625 мм | 63 | 950 мм | скрытые защелки |
| ALW-L-950х650-Z-АА | 0.371 м² | 945 мм | 650 мм | 65 | 950 мм | скрытые защелки |
| ALW-L-1000х100-Z-АА | 0.060 м² | 995 мм | 100 мм | 10 | 1000 мм | скрытые защелки |
| ALW-L-1000х125-Z-АА | 0.075 м² | 995 мм | 125 мм | 13 | 1000 мм | скрытые защелки |
| ALW-L-1000х150-Z-АА | 0.090 м² | 995 мм | 150 мм | 15 | 1000 мм | скрытые защелки |
| ALW-L-1000х200-Z-АА | 0.120 м² | 995 мм | 200 мм | 20 | 1000 мм | скрытые защелки |
| ALW-L-1000х225-Z-АА | 0.135 м² | 995 мм | 225 мм | 23 | 1000 мм | скрытые защелки |
| ALW-L-1000х250-Z-АА | 0.150 м² | 995 мм | 250 мм | 25 | 1000 мм | скрытые защелки |
| ALW-L-1000х300-Z-АА | 0.180 м² | 995 мм | 300 мм | 30 | 1000 мм | скрытые защелки |
| ALW-L-1000х325-Z-АА | 0.196 м² | 995 мм | 325 мм | 33 | 1000 мм | скрытые защелки |
| ALW-L-1000х350-Z-АА | 0.211 м² | 995 мм | 350 мм | 35 | 1000 мм | скрытые защелки |
| ALW-L-1000х400-Z-АА | 0.241 м² | 995 мм | 400 мм | 40 | 1000 мм | скрытые защелки |
| ALW-L-1000х425-Z-АА | 0.256 м² | 995 мм | 425 мм | 43 | 1000 мм | скрытые защелки |
| ALW-L-1000х450-Z-АА | 0.271 м² | 995 мм | 450 мм | 45 | 1000 мм | скрытые защелки |
| ALW-L-1000х500-Z-АА | 0.301 м² | 995 мм | 500 мм | 50 | 1000 мм | скрытые защелки |
| ALW-L-1000х525-Z-АА | 0.316 м² | 995 мм | 525 мм | 53 | 1000 мм | скрытые защелки |
| ALW-L-1000х550-Z-АА | 0.331 м² | 995 мм | 550 мм | 55 | 1000 мм | скрытые защелки |
| ALW-L-1000х600-Z-АА | 0.361 м² | 995 мм | 600 мм | 60 | 1000 мм | скрытые защелки |
| ALW-L-1000х625-Z-АА | 0.376 м² | 995 мм | 625 мм | 63 | 1000 мм | скрытые защелки |
| ALW-L-1000х650-Z-АА | 0.391 м² | 995 мм | 650 мм | 65 | 1000 мм | скрытые защелки |
| ALW-L-1025х100-Z-АА | 0.062 м² | 1020 мм | 100 мм | 10 | 1025 мм | скрытые защелки |
| ALW-L-1025х125-Z-АА | 0.077 м² | 1020 мм | 125 мм | 13 | 1025 мм | скрытые защелки |
| ALW-L-1025х150-Z-АА | 0.092 м² | 1020 мм | 150 мм | 15 | 1025 мм | скрытые защелки |
| ALW-L-1025х200-Z-АА | 0.123 м² | 1020 мм | 200 мм | 20 | 1025 мм | скрытые защелки |
| ALW-L-1025х225-Z-АА | 0.139 м² | 1020 мм | 225 мм | 23 | 1025 мм | скрытые защелки |
| ALW-L-1025х250-Z-АА | 0.154 м² | 1020 мм | 250 мм | 25 | 1025 мм | скрытые защелки |
| ALW-L-1025х300-Z-АА | 0.185 м² | 1020 мм | 300 мм | 30 | 1025 мм | скрытые защелки |
| ALW-L-1025х325-Z-АА | 0.200 м² | 1020 мм | 325 мм | 33 | 1025 мм | скрытые защелки |
| ALW-L-1025х350-Z-АА | 0.216 м² | 1020 мм | 350 мм | 35 | 1025 мм | скрытые защелки |
| ALW-L-1025х400-Z-АА | 0.247 м² | 1020 мм | 400 мм | 40 | 1025 мм | скрытые защелки |
| ALW-L-1025х425-Z-АА | 0.262 м² | 1020 мм | 425 мм | 43 | 1025 мм | скрытые защелки |
| ALW-L-1025х450-Z-АА | 0.277 м² | 1020 мм | 450 мм | 45 | 1025 мм | скрытые защелки |
| ALW-L-1025х500-Z-АА | 0.308 м² | 1020 мм | 500 мм | 50 | 1025 мм | скрытые защелки |
| ALW-L-1025х525-Z-АА | 0.324 м² | 1020 мм | 525 мм | 53 | 1025 мм | скрытые защелки |
| ALW-L-1025х550-Z-АА | 0.339 м² | 1020 мм | 550 мм | 55 | 1025 мм | скрытые защелки |
| ALW-L-1025х600-Z-АА | 0.370 м² | 1020 мм | 600 мм | 60 | 1025 мм | скрытые защелки |
| ALW-L-1025х625-Z-АА | 0.385 м² | 1020 мм | 625 мм | 63 | 1025 мм | скрытые защелки |
| ALW-L-1025х650-Z-АА | 0.401 м² | 1020 мм | 650 мм | 65 | 1025 мм | скрытые защелки |
| ALW-L-1050х100-Z-АА | 0.063 м² | 1045 мм | 100 мм | 10 | 1050 мм | скрытые защелки |
| ALW-L-1050х125-Z-АА | 0.079 м² | 1045 мм | 125 мм | 13 | 1050 мм | скрытые защелки |
| ALW-L-1050х150-Z-АА | 0.095 м² | 1045 мм | 150 мм | 15 | 1050 мм | скрытые защелки |
| ALW-L-1050х200-Z-АА | 0.126 м² | 1045 мм | 200 мм | 20 | 1050 мм | скрытые защелки |
| ALW-L-1050х225-Z-АА | 0.142 м² | 1045 мм | 225 мм | 23 | 1050 мм | скрытые защелки |
| ALW-L-1050х250-Z-АА | 0.158 м² | 1045 мм | 250 мм | 25 | 1050 мм | скрытые защелки |
| ALW-L-1050х300-Z-АА | 0.190 м² | 1045 мм | 300 мм | 30 | 1050 мм | скрытые защелки |
| ALW-L-1050х325-Z-АА | 0.205 м² | 1045 мм | 325 мм | 33 | 1050 мм | скрытые защелки |
| ALW-L-1050х350-Z-АА | 0.221 м² | 1045 мм | 350 мм | 35 | 1050 мм | скрытые защелки |
| ALW-L-1050х400-Z-АА | 0.253 м² | 1045 мм | 400 мм | 40 | 1050 мм | скрытые защелки |
| ALW-L-1050х425-Z-АА | 0.268 м² | 1045 мм | 425 мм | 43 | 1050 мм | скрытые защелки |
| ALW-L-1050х450-Z-АА | 0.284 м² | 1045 мм | 450 мм | 45 | 1050 мм | скрытые защелки |
| ALW-L-1050х500-Z-АА | 0.316 м² | 1045 мм | 500 мм | 50 | 1050 мм | скрытые защелки |
| ALW-L-1050х525-Z-АА | 0.332 м² | 1045 мм | 525 мм | 53 | 1050 мм | скрытые защелки |
| ALW-L-1050х550-Z-АА | 0.347 м² | 1045 мм | 550 мм | 55 | 1050 мм | скрытые защелки |
| ALW-L-1050х600-Z-АА | 0.379 м² | 1045 мм | 600 мм | 60 | 1050 мм | скрытые защелки |
| ALW-L-1050х625-Z-АА | 0.395 м² | 1045 мм | 625 мм | 63 | 1050 мм | скрытые защелки |
| ALW-L-1050х650-Z-АА | 0.411 м² | 1045 мм | 650 мм | 65 | 1050 мм | скрытые защелки |
| ALW-L-1100х100-Z-АА | 0.066 м² | 1095 мм | 100 мм | 10 | 1100 мм | скрытые защелки |
| ALW-L-1100х125-Z-АА | 0.083 м² | 1095 мм | 125 мм | 13 | 1100 мм | скрытые защелки |
| ALW-L-1100х150-Z-АА | 0.099 м² | 1095 мм | 150 мм | 15 | 1100 мм | скрытые защелки |
| ALW-L-1100х200-Z-АА | 0.132 м² | 1095 мм | 200 мм | 20 | 1100 мм | скрытые защелки |
| ALW-L-1100х225-Z-АА | 0.149 м² | 1095 мм | 225 мм | 23 | 1100 мм | скрытые защелки |
| ALW-L-1100х250-Z-АА | 0.165 м² | 1095 мм | 250 мм | 25 | 1100 мм | скрытые защелки |
| ALW-L-1100х300-Z-АА | 0.199 м² | 1095 мм | 300 мм | 30 | 1100 мм | скрытые защелки |
| ALW-L-1100х325-Z-АА | 0.215 м² | 1095 мм | 325 мм | 33 | 1100 мм | скрытые защелки |
| ALW-L-1100х350-Z-АА | 0.232 м² | 1095 мм | 350 мм | 35 | 1100 мм | скрытые защелки |
| ALW-L-1100х400-Z-АА | 0.265 м² | 1095 мм | 400 мм | 40 | 1100 мм | скрытые защелки |
| ALW-L-1100х425-Z-АА | 0.281 м² | 1095 мм | 425 мм | 43 | 1100 мм | скрытые защелки |
| ALW-L-1100х450-Z-АА | 0.298 м² | 1095 мм | 450 мм | 45 | 1100 мм | скрытые защелки |
| ALW-L-1100х500-Z-АА | 0.331 м² | 1095 мм | 500 мм | 50 | 1100 мм | скрытые защелки |
| ALW-L-1100х525-Z-АА | 0.347 м² | 1095 мм | 525 мм | 53 | 1100 мм | скрытые защелки |
| ALW-L-1100х550-Z-АА | 0.364 м² | 1095 мм | 550 мм | 55 | 1100 мм | скрытые защелки |
| ALW-L-1100х600-Z-АА | 0.397 м² | 1095 мм | 600 мм | 60 | 1100 мм | скрытые защелки |
| ALW-L-1100х625-Z-АА | 0.414 м² | 1095 мм | 625 мм | 63 | 1100 мм | скрытые защелки |
| ALW-L-1100х650-Z-АА | 0.430 м² | 1095 мм | 650 мм | 65 | 1100 мм | скрытые защелки |
| ALW-L-1125х100-Z-АА | 0.068 м² | 1120 мм | 100 мм | 10 | 1125 мм | скрытые защелки |
| ALW-L-1125х125-Z-АА | 0.085 м² | 1120 мм | 125 мм | 13 | 1125 мм | скрытые защелки |
| ALW-L-1125х150-Z-АА | 0.102 м² | 1120 мм | 150 мм | 15 | 1125 мм | скрытые защелки |
| ALW-L-1125х200-Z-АА | 0.135 м² | 1120 мм | 200 мм | 20 | 1125 мм | скрытые защелки |
| ALW-L-1125х225-Z-АА | 0.152 м² | 1120 мм | 225 мм | 23 | 1125 мм | скрытые защелки |
| ALW-L-1125х250-Z-АА | 0.169 м² | 1120 мм | 250 мм | 25 | 1125 мм | скрытые защелки |
| ALW-L-1125х300-Z-АА | 0.203 м² | 1120 мм | 300 мм | 30 | 1125 мм | скрытые защелки |
| ALW-L-1125х325-Z-АА | 0.220 м² | 1120 мм | 325 мм | 33 | 1125 мм | скрытые защелки |
| ALW-L-1125х350-Z-АА | 0.237 м² | 1120 мм | 350 мм | 35 | 1125 мм | скрытые защелки |
| ALW-L-1125х400-Z-АА | 0.271 м² | 1120 мм | 400 мм | 40 | 1125 мм | скрытые защелки |
| ALW-L-1125х425-Z-АА | 0.288 м² | 1120 мм | 425 мм | 43 | 1125 мм | скрытые защелки |
| ALW-L-1125х450-Z-АА | 0.305 м² | 1120 мм | 450 мм | 45 | 1125 мм | скрытые защелки |
| ALW-L-1125х500-Z-АА | 0.338 м² | 1120 мм | 500 мм | 50 | 1125 мм | скрытые защелки |
| ALW-L-1125х525-Z-АА | 0.355 м² | 1120 мм | 525 мм | 53 | 1125 мм | скрытые защелки |
| ALW-L-1125х550-Z-АА | 0.372 м² | 1120 мм | 550 мм | 55 | 1125 мм | скрытые защелки |
| ALW-L-1125х600-Z-АА | 0.406 м² | 1120 мм | 600 мм | 60 | 1125 мм | скрытые защелки |
| ALW-L-1125х625-Z-АА | 0.423 м² | 1120 мм | 625 мм | 63 | 1125 мм | скрытые защелки |
| ALW-L-1125х650-Z-АА | 0.440 м² | 1120 мм | 650 мм | 65 | 1125 мм | скрытые защелки |
| ALW-L-1150х100-Z-АА | 0.069 м² | 1145 мм | 100 мм | 10 | 1150 мм | скрытые защелки |
| ALW-L-1150х125-Z-АА | 0.086 м² | 1145 мм | 125 мм | 13 | 1150 мм | скрытые защелки |
| ALW-L-1150х150-Z-АА | 0.104 м² | 1145 мм | 150 мм | 15 | 1150 мм | скрытые защелки |
| ALW-L-1150х200-Z-АА | 0.138 м² | 1145 мм | 200 мм | 20 | 1150 мм | скрытые защелки |
| ALW-L-1150х225-Z-АА | 0.156 м² | 1145 мм | 225 мм | 23 | 1150 мм | скрытые защелки |
| ALW-L-1150х250-Z-АА | 0.173 м² | 1145 мм | 250 мм | 25 | 1150 мм | скрытые защелки |
| ALW-L-1150х300-Z-АА | 0.208 м² | 1145 мм | 300 мм | 30 | 1150 мм | скрытые защелки |
| ALW-L-1150х325-Z-АА | 0.225 м² | 1145 мм | 325 мм | 33 | 1150 мм | скрытые защелки |
| ALW-L-1150х350-Z-АА | 0.242 м² | 1145 мм | 350 мм | 35 | 1150 мм | скрытые защелки |
| ALW-L-1150х400-Z-АА | 0.277 м² | 1145 мм | 400 мм | 40 | 1150 мм | скрытые защелки |
| ALW-L-1150х425-Z-АА | 0.294 м² | 1145 мм | 425 мм | 43 | 1150 мм | скрытые защелки |
| ALW-L-1150х450-Z-АА | 0.311 м² | 1145 мм | 450 мм | 45 | 1150 мм | скрытые защелки |
| ALW-L-1150х500-Z-АА | 0.346 м² | 1145 мм | 500 мм | 50 | 1150 мм | скрытые защелки |
| ALW-L-1150х525-Z-АА | 0.363 м² | 1145 мм | 525 мм | 53 | 1150 мм | скрытые защелки |
| ALW-L-1150х550-Z-АА | 0.381 м² | 1145 мм | 550 мм | 55 | 1150 мм | скрытые защелки |
| ALW-L-1150х600-Z-АА | 0.415 м² | 1145 мм | 600 мм | 60 | 1150 мм | скрытые защелки |
| ALW-L-1150х625-Z-АА | 0.432 м² | 1145 мм | 625 мм | 63 | 1150 мм | скрытые защелки |
| ALW-L-1150х650-Z-АА | 0.450 м² | 1145 мм | 650 мм | 65 | 1150 мм | скрытые защелки |
| ALW-L-1200х100-Z-АА | 0.072 м² | 1195 мм | 100 мм | 10 | 1200 мм | скрытые защелки |
| ALW-L-1200х125-Z-АА | 0.090 м² | 1195 мм | 125 мм | 13 | 1200 мм | скрытые защелки |
| ALW-L-1200х150-Z-АА | 0.108 м² | 1195 мм | 150 мм | 15 | 1200 мм | скрытые защелки |
| ALW-L-1200х200-Z-АА | 0.144 м² | 1195 мм | 200 мм | 20 | 1200 мм | скрытые защелки |
| ALW-L-1200х225-Z-АА | 0.162 м² | 1195 мм | 225 мм | 23 | 1200 мм | скрытые защелки |
| ALW-L-1200х250-Z-АА | 0.180 м² | 1195 мм | 250 мм | 25 | 1200 мм | скрытые защелки |
| ALW-L-1200х300-Z-АА | 0.217 м² | 1195 мм | 300 мм | 30 | 1200 мм | скрытые защелки |
| ALW-L-1200х325-Z-АА | 0.235 м² | 1195 мм | 325 мм | 33 | 1200 мм | скрытые защелки |
| ALW-L-1200х350-Z-АА | 0.253 м² | 1195 мм | 350 мм | 35 | 1200 мм | скрытые защелки |
| ALW-L-1200х400-Z-АА | 0.289 м² | 1195 мм | 400 мм | 40 | 1200 мм | скрытые защелки |
| ALW-L-1200х425-Z-АА | 0.307 м² | 1195 мм | 425 мм | 43 | 1200 мм | скрытые защелки |
| ALW-L-1200х450-Z-АА | 0.325 м² | 1195 мм | 450 мм | 45 | 1200 мм | скрытые защелки |
| ALW-L-1200х500-Z-АА | 0.361 м² | 1195 мм | 500 мм | 50 | 1200 мм | скрытые защелки |
| ALW-L-1200х525-Z-АА | 0.379 м² | 1195 мм | 525 мм | 53 | 1200 мм | скрытые защелки |
| ALW-L-1200х550-Z-АА | 0.397 м² | 1195 мм | 550 мм | 55 | 1200 мм | скрытые защелки |
| ALW-L-1200х600-Z-АА | 0.433 м² | 1195 мм | 600 мм | 60 | 1200 мм | скрытые защелки |
| ALW-L-1200х625-Z-АА | 0.451 м² | 1195 мм | 625 мм | 63 | 1200 мм | скрытые защелки |
| ALW-L-1200х650-Z-АА | 0.469 м² | 1195 мм | 650 мм | 65 | 1200 мм | скрытые защелки |
| ALW-L-1225х100-Z-АА | 0.074 м² | 1220 мм | 100 мм | 10 | 1225 мм | скрытые защелки |
| ALW-L-1225х125-Z-АА | 0.092 м² | 1220 мм | 125 мм | 13 | 1225 мм | скрытые защелки |
| ALW-L-1225х150-Z-АА | 0.111 м² | 1220 мм | 150 мм | 15 | 1225 мм | скрытые защелки |
| ALW-L-1225х200-Z-АА | 0.147 м² | 1220 мм | 200 мм | 20 | 1225 мм | скрытые защелки |
| ALW-L-1225х225-Z-АА | 0.166 м² | 1220 мм | 225 мм | 23 | 1225 мм | скрытые защелки |
| ALW-L-1225х250-Z-АА | 0.184 м² | 1220 мм | 250 мм | 25 | 1225 мм | скрытые защелки |
| ALW-L-1225х300-Z-АА | 0.221 м² | 1220 мм | 300 мм | 30 | 1225 мм | скрытые защелки |
| ALW-L-1225х325-Z-АА | 0.240 м² | 1220 мм | 325 мм | 33 | 1225 мм | скрытые защелки |
| ALW-L-1225х350-Z-АА | 0.258 м² | 1220 мм | 350 мм | 35 | 1225 мм | скрытые защелки |
| ALW-L-1225х400-Z-АА | 0.295 м² | 1220 мм | 400 мм | 40 | 1225 мм | скрытые защелки |
| ALW-L-1225х425-Z-АА | 0.313 м² | 1220 мм | 425 мм | 43 | 1225 мм | скрытые защелки |
| ALW-L-1225х450-Z-АА | 0.332 м² | 1220 мм | 450 мм | 45 | 1225 мм | скрытые защелки |
| ALW-L-1225х500-Z-АА | 0.368 м² | 1220 мм | 500 мм | 50 | 1225 мм | скрытые защелки |
| ALW-L-1225х525-Z-АА | 0.387 м² | 1220 мм | 525 мм | 53 | 1225 мм | скрытые защелки |
| ALW-L-1225х550-Z-АА | 0.405 м² | 1220 мм | 550 мм | 55 | 1225 мм | скрытые защелки |
| ALW-L-1225х600-Z-АА | 0.442 м² | 1220 мм | 600 мм | 60 | 1225 мм | скрытые защелки |
| ALW-L-1225х625-Z-АА | 0.461 м² | 1220 мм | 625 мм | 63 | 1225 мм | скрытые защелки |
| ALW-L-1225х650-Z-АА | 0.479 м² | 1220 мм | 650 мм | 65 | 1225 мм | скрытые защелки |
| ALW-L-1250х100-Z-АА | 0.075 м² | 1245 мм | 100 мм | 10 | 1250 мм | скрытые защелки |
| ALW-L-1250х125-Z-АА | 0.094 м² | 1245 мм | 125 мм | 13 | 1250 мм | скрытые защелки |
| ALW-L-1250х150-Z-АА | 0.113 м² | 1245 мм | 150 мм | 15 | 1250 мм | скрытые защелки |
| ALW-L-1250х200-Z-АА | 0.150 м² | 1245 мм | 200 мм | 20 | 1250 мм | скрытые защелки |
| ALW-L-1250х225-Z-АА | 0.169 м² | 1245 мм | 225 мм | 23 | 1250 мм | скрытые защелки |
| ALW-L-1250х250-Z-АА | 0.188 м² | 1245 мм | 250 мм | 25 | 1250 мм | скрытые защелки |
| ALW-L-1250х300-Z-АА | 0.226 м² | 1245 мм | 300 мм | 30 | 1250 мм | скрытые защелки |
| ALW-L-1250х325-Z-АА | 0.244 м² | 1245 мм | 325 мм | 33 | 1250 мм | скрытые защелки |
| ALW-L-1250х350-Z-АА | 0.263 м² | 1245 мм | 350 мм | 35 | 1250 мм | скрытые защелки |
| ALW-L-1250х400-Z-АА | 0.301 м² | 1245 мм | 400 мм | 40 | 1250 мм | скрытые защелки |
| ALW-L-1250х425-Z-АА | 0.320 м² | 1245 мм | 425 мм | 43 | 1250 мм | скрытые защелки |
| ALW-L-1250х450-Z-АА | 0.338 м² | 1245 мм | 450 мм | 45 | 1250 мм | скрытые защелки |
| ALW-L-1250х500-Z-АА | 0.376 м² | 1245 мм | 500 мм | 50 | 1250 мм | скрытые защелки |
| ALW-L-1250х525-Z-АА | 0.395 м² | 1245 мм | 525 мм | 53 | 1250 мм | скрытые защелки |
| ALW-L-1250х550-Z-АА | 0.414 м² | 1245 мм | 550 мм | 55 | 1250 мм | скрытые защелки |
| ALW-L-1250х600-Z-АА | 0.451 м² | 1245 мм | 600 мм | 60 | 1250 мм | скрытые защелки |
| ALW-L-1250х625-Z-АА | 0.470 м² | 1245 мм | 625 мм | 63 | 1250 мм | скрытые защелки |
| ALW-L-1250х650-Z-АА | 0.489 м² | 1245 мм | 650 мм | 65 | 1250 мм | скрытые защелки |
| ALW-L-1300х100-Z-АА | 0.078 м² | 1295 мм | 100 мм | 10 | 1300 мм | скрытые защелки |
| ALW-L-1300х125-Z-АА | 0.098 м² | 1295 мм | 125 мм | 13 | 1300 мм | скрытые защелки |
| ALW-L-1300х150-Z-АА | 0.117 м² | 1295 мм | 150 мм | 15 | 1300 мм | скрытые защелки |
| ALW-L-1300х200-Z-АА | 0.156 м² | 1295 мм | 200 мм | 20 | 1300 мм | скрытые защелки |
| ALW-L-1300х225-Z-АА | 0.176 м² | 1295 мм | 225 мм | 23 | 1300 мм | скрытые защелки |
| ALW-L-1300х250-Z-АА | 0.196 м² | 1295 мм | 250 мм | 25 | 1300 мм | скрытые защелки |
| ALW-L-1300х300-Z-АА | 0.235 м² | 1295 мм | 300 мм | 30 | 1300 мм | скрытые защелки |
| ALW-L-1300х325-Z-АА | 0.254 м² | 1295 мм | 325 мм | 33 | 1300 мм | скрытые защелки |
| ALW-L-1300х350-Z-АА | 0.274 м² | 1295 мм | 350 мм | 35 | 1300 мм | скрытые защелки |
| ALW-L-1300х400-Z-АА | 0.313 м² | 1295 мм | 400 мм | 40 | 1300 мм | скрытые защелки |
| ALW-L-1300х425-Z-АА | 0.332 м² | 1295 мм | 425 мм | 43 | 1300 мм | скрытые защелки |
| ALW-L-1300х450-Z-АА | 0.352 м² | 1295 мм | 450 мм | 45 | 1300 мм | скрытые защелки |
| ALW-L-1300х500-Z-АА | 0.391 м² | 1295 мм | 500 мм | 50 | 1300 мм | скрытые защелки |
| ALW-L-1300х525-Z-АА | 0.411 м² | 1295 мм | 525 мм | 53 | 1300 мм | скрытые защелки |
| ALW-L-1300х550-Z-АА | 0.430 м² | 1295 мм | 550 мм | 55 | 1300 мм | скрытые защелки |
| ALW-L-1300х600-Z-АА | 0.469 м² | 1295 мм | 600 мм | 60 | 1300 мм | скрытые защелки |
| ALW-L-1300х625-Z-АА | 0.489 м² | 1295 мм | 625 мм | 63 | 1300 мм | скрытые защелки |
| ALW-L-1300х650-Z-АА | 0.508 м² | 1295 мм | 650 мм | 65 | 1300 мм | скрытые защелки |
| ALW-L-1325х100-Z-АА | 0.080 м² | 1320 мм | 100 мм | 10 | 1325 мм | скрытые защелки |
| ALW-L-1325х125-Z-АА | 0.100 м² | 1320 мм | 125 мм | 13 | 1325 мм | скрытые защелки |
| ALW-L-1325х150-Z-АА | 0.120 м² | 1320 мм | 150 мм | 15 | 1325 мм | скрытые защелки |
| ALW-L-1325х200-Z-АА | 0.159 м² | 1320 мм | 200 мм | 20 | 1325 мм | скрытые защелки |
| ALW-L-1325х225-Z-АА | 0.179 м² | 1320 мм | 225 мм | 23 | 1325 мм | скрытые защелки |
| ALW-L-1325х250-Z-АА | 0.199 м² | 1320 мм | 250 мм | 25 | 1325 мм | скрытые защелки |
| ALW-L-1325х300-Z-АА | 0.239 м² | 1320 мм | 300 мм | 30 | 1325 мм | скрытые защелки |
| ALW-L-1325х325-Z-АА | 0.259 м² | 1320 мм | 325 мм | 33 | 1325 мм | скрытые защелки |
| ALW-L-1325х350-Z-АА | 0.279 м² | 1320 мм | 350 мм | 35 | 1325 мм | скрытые защелки |
| ALW-L-1325х400-Z-АА | 0.319 м² | 1320 мм | 400 мм | 40 | 1325 мм | скрытые защелки |
| ALW-L-1325х425-Z-АА | 0.339 м² | 1320 мм | 425 мм | 43 | 1325 мм | скрытые защелки |
| ALW-L-1325х450-Z-АА | 0.359 м² | 1320 мм | 450 мм | 45 | 1325 мм | скрытые защелки |
| ALW-L-1325х500-Z-АА | 0.399 м² | 1320 мм | 500 мм | 50 | 1325 мм | скрытые защелки |
| ALW-L-1325х525-Z-АА | 0.418 м² | 1320 мм | 525 мм | 53 | 1325 мм | скрытые защелки |
| ALW-L-1325х550-Z-АА | 0.438 м² | 1320 мм | 550 мм | 55 | 1325 мм | скрытые защелки |
| ALW-L-1325х600-Z-АА | 0.478 м² | 1320 мм | 600 мм | 60 | 1325 мм | скрытые защелки |
| ALW-L-1325х625-Z-АА | 0.498 м² | 1320 мм | 625 мм | 63 | 1325 мм | скрытые защелки |
| ALW-L-1325х650-Z-АА | 0.518 м² | 1320 мм | 650 мм | 65 | 1325 мм | скрытые защелки |
| ALW-L-1350х100-Z-АА | 0.081 м² | 1345 мм | 100 мм | 10 | 1350 мм | скрытые защелки |
| ALW-L-1350х125-Z-АА | 0.102 м² | 1345 мм | 125 мм | 13 | 1350 мм | скрытые защелки |
| ALW-L-1350х150-Z-АА | 0.122 м² | 1345 мм | 150 мм | 15 | 1350 мм | скрытые защелки |
| ALW-L-1350х200-Z-АА | 0.162 м² | 1345 мм | 200 мм | 20 | 1350 мм | скрытые защелки |
| ALW-L-1350х225-Z-АА | 0.183 м² | 1345 мм | 225 мм | 23 | 1350 мм | скрытые защелки |
| ALW-L-1350х250-Z-АА | 0.203 м² | 1345 мм | 250 мм | 25 | 1350 мм | скрытые защелки |
| ALW-L-1350х300-Z-АА | 0.244 м² | 1345 мм | 300 мм | 30 | 1350 мм | скрытые защелки |
| ALW-L-1350х325-Z-АА | 0.264 м² | 1345 мм | 325 мм | 33 | 1350 мм | скрытые защелки |
| ALW-L-1350х350-Z-АА | 0.284 м² | 1345 мм | 350 мм | 35 | 1350 мм | скрытые защелки |
| ALW-L-1350х400-Z-АА | 0.325 м² | 1345 мм | 400 мм | 40 | 1350 мм | скрытые защелки |
| ALW-L-1350х425-Z-АА | 0.345 м² | 1345 мм | 425 мм | 43 | 1350 мм | скрытые защелки |
| ALW-L-1350х450-Z-АА | 0.365 м² | 1345 мм | 450 мм | 45 | 1350 мм | скрытые защелки |
| ALW-L-1350х500-Z-АА | 0.406 м² | 1345 мм | 500 мм | 50 | 1350 мм | скрытые защелки |
| ALW-L-1350х525-Z-АА | 0.426 м² | 1345 мм | 525 мм | 53 | 1350 мм | скрытые защелки |
| ALW-L-1350х550-Z-АА | 0.447 м² | 1345 мм | 550 мм | 55 | 1350 мм | скрытые защелки |
| ALW-L-1350х600-Z-АА | 0.487 м² | 1345 мм | 600 мм | 60 | 1350 мм | скрытые защелки |
| ALW-L-1350х625-Z-АА | 0.508 м² | 1345 мм | 625 мм | 63 | 1350 мм | скрытые защелки |
| ALW-L-1350х650-Z-АА | 0.528 м² | 1345 мм | 650 мм | 65 | 1350 мм | скрытые защелки |
| ALW-L-1400х100-Z-АА | 0.084 м² | 1395 мм | 100 мм | 10 | 1400 мм | скрытые защелки |
| ALW-L-1400х125-Z-АА | 0.105 м² | 1395 мм | 125 мм | 13 | 1400 мм | скрытые защелки |
| ALW-L-1400х150-Z-АА | 0.126 м² | 1395 мм | 150 мм | 15 | 1400 мм | скрытые защелки |
| ALW-L-1400х200-Z-АА | 0.168 м² | 1395 мм | 200 мм | 20 | 1400 мм | скрытые защелки |
| ALW-L-1400х225-Z-АА | 0.190 м² | 1395 мм | 225 мм | 23 | 1400 мм | скрытые защелки |
| ALW-L-1400х250-Z-АА | 0.211 м² | 1395 мм | 250 мм | 25 | 1400 мм | скрытые защелки |
| ALW-L-1400х300-Z-АА | 0.253 м² | 1395 мм | 300 мм | 30 | 1400 мм | скрытые защелки |
| ALW-L-1400х325-Z-АА | 0.274 м² | 1395 мм | 325 мм | 33 | 1400 мм | скрытые защелки |
| ALW-L-1400х350-Z-АА | 0.295 м² | 1395 мм | 350 мм | 35 | 1400 мм | скрытые защелки |
| ALW-L-1400х400-Z-АА | 0.337 м² | 1395 мм | 400 мм | 40 | 1400 мм | скрытые защелки |
| ALW-L-1400х425-Z-АА | 0.358 м² | 1395 мм | 425 мм | 43 | 1400 мм | скрытые защелки |
| ALW-L-1400х450-Z-АА | 0.379 м² | 1395 мм | 450 мм | 45 | 1400 мм | скрытые защелки |
| ALW-L-1400х500-Z-АА | 0.421 м² | 1395 мм | 500 мм | 50 | 1400 мм | скрытые защелки |
| ALW-L-1400х525-Z-АА | 0.442 м² | 1395 мм | 525 мм | 53 | 1400 мм | скрытые защелки |
| ALW-L-1400х550-Z-АА | 0.463 м² | 1395 мм | 550 мм | 55 | 1400 мм | скрытые защелки |
| ALW-L-1400х600-Z-АА | 0.505 м² | 1395 мм | 600 мм | 60 | 1400 мм | скрытые защелки |
| ALW-L-1400х625-Z-АА | 0.526 м² | 1395 мм | 625 мм | 63 | 1400 мм | скрытые защелки |
| ALW-L-1400х650-Z-АА | 0.547 м² | 1395 мм | 650 мм | 65 | 1400 мм | скрытые защелки |
| ALW-L-1425х100-Z-АА | 0.086 м² | 1420 мм | 100 мм | 10 | 1425 мм | скрытые защелки |
| ALW-L-1425х125-Z-АА | 0.107 м² | 1420 мм | 125 мм | 13 | 1425 мм | скрытые защелки |
| ALW-L-1425х150-Z-АА | 0.129 м² | 1420 мм | 150 мм | 15 | 1425 мм | скрытые защелки |
| ALW-L-1425х200-Z-АА | 0.171 м² | 1420 мм | 200 мм | 20 | 1425 мм | скрытые защелки |
| ALW-L-1425х225-Z-АА | 0.193 м² | 1420 мм | 225 мм | 23 | 1425 мм | скрытые защелки |
| ALW-L-1425х250-Z-АА | 0.214 м² | 1420 мм | 250 мм | 25 | 1425 мм | скрытые защелки |
| ALW-L-1425х300-Z-АА | 0.257 м² | 1420 мм | 300 мм | 30 | 1425 мм | скрытые защелки |
| ALW-L-1425х325-Z-АА | 0.279 м² | 1420 мм | 325 мм | 33 | 1425 мм | скрытые защелки |
| ALW-L-1425х350-Z-АА | 0.300 м² | 1420 мм | 350 мм | 35 | 1425 мм | скрытые защелки |
| ALW-L-1425х400-Z-АА | 0.343 м² | 1420 мм | 400 мм | 40 | 1425 мм | скрытые защелки |
| ALW-L-1425х425-Z-АА | 0.364 м² | 1420 мм | 425 мм | 43 | 1425 мм | скрытые защелки |
| ALW-L-1425х450-Z-АА | 0.386 м² | 1420 мм | 450 мм | 45 | 1425 мм | скрытые защелки |
| ALW-L-1425х500-Z-АА | 0.429 м² | 1420 мм | 500 мм | 50 | 1425 мм | скрытые защелки |
| ALW-L-1425х525-Z-АА | 0.450 м² | 1420 мм | 525 мм | 53 | 1425 мм | скрытые защелки |
| ALW-L-1425х550-Z-АА | 0.472 м² | 1420 мм | 550 мм | 55 | 1425 мм | скрытые защелки |
| ALW-L-1425х600-Z-АА | 0.514 м² | 1420 мм | 600 мм | 60 | 1425 мм | скрытые защелки |
| ALW-L-1425х625-Z-АА | 0.536 м² | 1420 мм | 625 мм | 63 | 1425 мм | скрытые защелки |
| ALW-L-1425х650-Z-АА | 0.557 м² | 1420 мм | 650 мм | 65 | 1425 мм | скрытые защелки |
| ALW-L-1450х100-Z-АА | 0.087 м² | 1445 мм | 100 мм | 10 | 1450 мм | скрытые защелки |
| ALW-L-1450х125-Z-АА | 0.109 м² | 1445 мм | 125 мм | 13 | 1450 мм | скрытые защелки |
| ALW-L-1450х150-Z-АА | 0.131 м² | 1445 мм | 150 мм | 15 | 1450 мм | скрытые защелки |
| ALW-L-1450х200-Z-АА | 0.174 м² | 1445 мм | 200 мм | 20 | 1450 мм | скрытые защелки |
| ALW-L-1450х225-Z-АА | 0.196 м² | 1445 мм | 225 мм | 23 | 1450 мм | скрытые защелки |
| ALW-L-1450х250-Z-АА | 0.218 м² | 1445 мм | 250 мм | 25 | 1450 мм | скрытые защелки |
| ALW-L-1450х300-Z-АА | 0.262 м² | 1445 мм | 300 мм | 30 | 1450 мм | скрытые защелки |
| ALW-L-1450х325-Z-АА | 0.284 м² | 1445 мм | 325 мм | 33 | 1450 мм | скрытые защелки |
| ALW-L-1450х350-Z-АА | 0.305 м² | 1445 мм | 350 мм | 35 | 1450 мм | скрытые защелки |
| ALW-L-1450х400-Z-АА | 0.349 м² | 1445 мм | 400 мм | 40 | 1450 мм | скрытые защелки |
| ALW-L-1450х425-Z-АА | 0.371 м² | 1445 мм | 425 мм | 43 | 1450 мм | скрытые защелки |
| ALW-L-1450х450-Z-АА | 0.393 м² | 1445 мм | 450 мм | 45 | 1450 мм | скрытые защелки |
| ALW-L-1450х500-Z-АА | 0.436 м² | 1445 мм | 500 мм | 50 | 1450 мм | скрытые защелки |
| ALW-L-1450х525-Z-АА | 0.458 м² | 1445 мм | 525 мм | 53 | 1450 мм | скрытые защелки |
| ALW-L-1450х550-Z-АА | 0.480 м² | 1445 мм | 550 мм | 55 | 1450 мм | скрытые защелки |
| ALW-L-1450х600-Z-АА | 0.523 м² | 1445 мм | 600 мм | 60 | 1450 мм | скрытые защелки |
| ALW-L-1450х625-Z-АА | 0.545 м² | 1445 мм | 625 мм | 63 | 1450 мм | скрытые защелки |
| ALW-L-1450х650-Z-АА | 0.567 м² | 1445 мм | 650 мм | 65 | 1450 мм | скрытые защелки |
| ALW-L-1500х100-Z-АА | 0.090 м² | 1495 мм | 100 мм | 10 | 1500 мм | скрытые защелки |
| ALW-L-1500х125-Z-АА | 0.113 м² | 1495 мм | 125 мм | 13 | 1500 мм | скрытые защелки |
| ALW-L-1500х150-Z-АА | 0.135 м² | 1495 мм | 150 мм | 15 | 1500 мм | скрытые защелки |
| ALW-L-1500х200-Z-АА | 0.180 м² | 1495 мм | 200 мм | 20 | 1500 мм | скрытые защелки |
| ALW-L-1500х225-Z-АА | 0.203 м² | 1495 мм | 225 мм | 23 | 1500 мм | скрытые защелки |
| ALW-L-1500х250-Z-АА | 0.226 м² | 1495 мм | 250 мм | 25 | 1500 мм | скрытые защелки |
| ALW-L-1500х300-Z-АА | 0.271 м² | 1495 мм | 300 мм | 30 | 1500 мм | скрытые защелки |
| ALW-L-1500х325-Z-АА | 0.293 м² | 1495 мм | 325 мм | 33 | 1500 мм | скрытые защелки |
| ALW-L-1500х350-Z-АА | 0.316 м² | 1495 мм | 350 мм | 35 | 1500 мм | скрытые защелки |
| ALW-L-1500х400-Z-АА | 0.361 м² | 1495 мм | 400 мм | 40 | 1500 мм | скрытые защелки |
| ALW-L-1500х425-Z-АА | 0.384 м² | 1495 мм | 425 мм | 43 | 1500 мм | скрытые защелки |
| ALW-L-1500х450-Z-АА | 0.406 м² | 1495 мм | 450 мм | 45 | 1500 мм | скрытые защелки |
| ALW-L-1500х500-Z-АА | 0.451 м² | 1495 мм | 500 мм | 50 | 1500 мм | скрытые защелки |
| ALW-L-1500х525-Z-АА | 0.474 м² | 1495 мм | 525 мм | 53 | 1500 мм | скрытые защелки |
| ALW-L-1500х550-Z-АА | 0.496 м² | 1495 мм | 550 мм | 55 | 1500 мм | скрытые защелки |
| ALW-L-1500х600-Z-АА | 0.541 м² | 1495 мм | 600 мм | 60 | 1500 мм | скрытые защелки |
| ALW-L-1500х625-Z-АА | 0.564 м² | 1495 мм | 625 мм | 63 | 1500 мм | скрытые защелки |
| ALW-L-1500х650-Z-АА | 0.587 м² | 1495 мм | 650 мм | 65 | 1500 мм | скрытые защелки |

note: column(s) folded — value = type name in every type: Комментарии к типоразмеру
